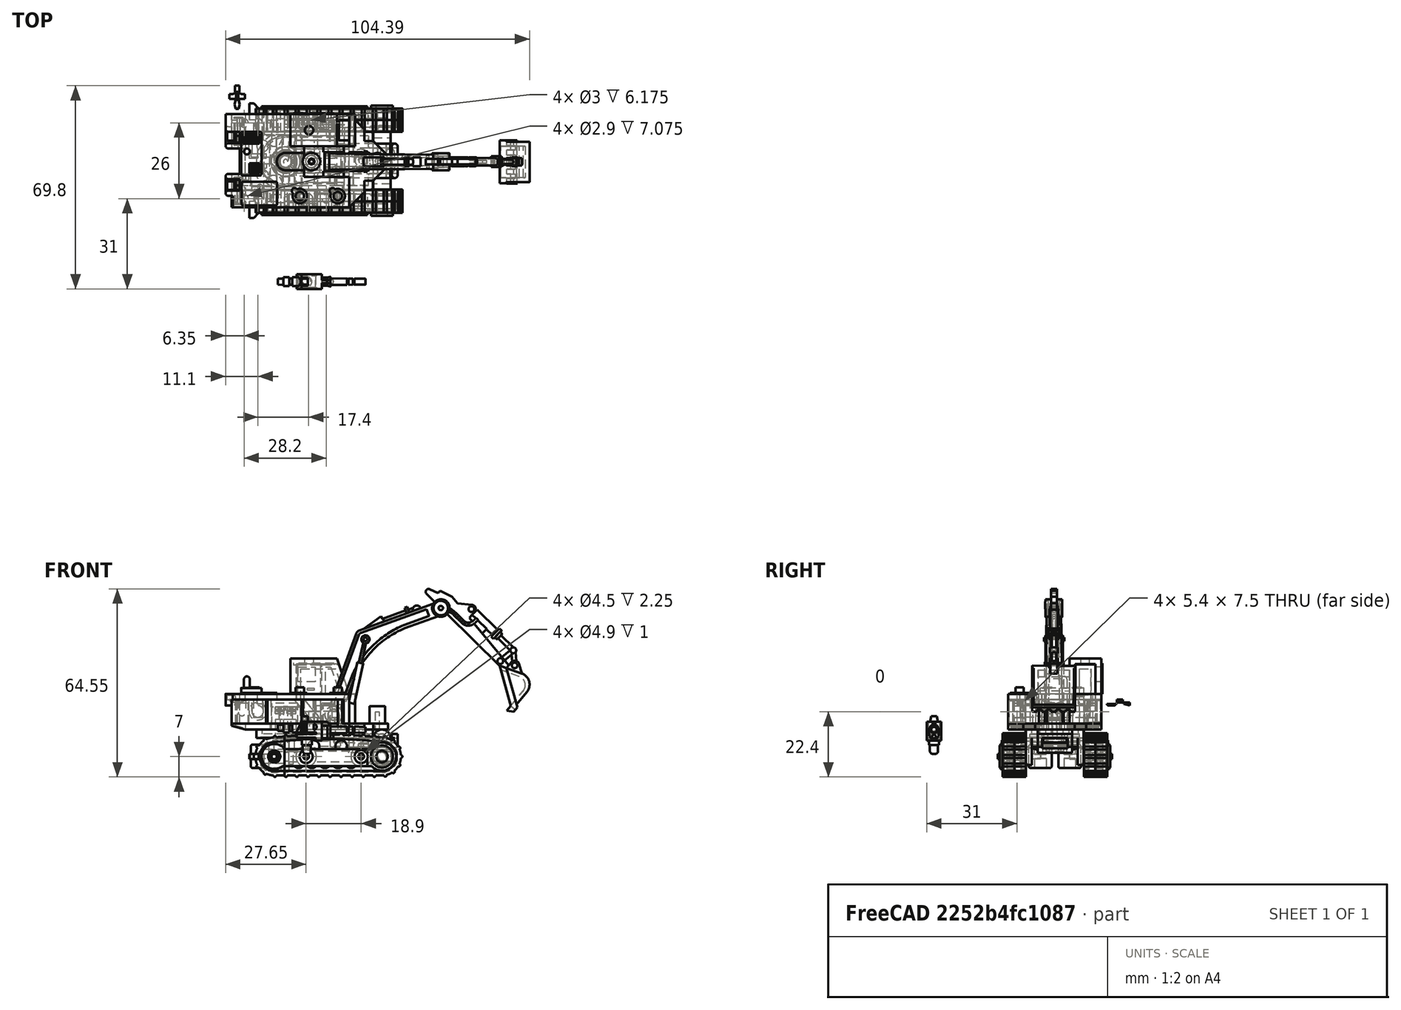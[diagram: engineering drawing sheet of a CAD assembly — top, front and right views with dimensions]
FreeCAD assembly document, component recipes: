
FREECAD ASSEMBLY — COMPONENT RECIPES ("Scavanger")

This assembly document has 15 components, labeled P0..P14 below (a component is one placed body or linked part). 15 of them carry a construction recipe — the FreeCAD feature program that regenerates the part from scratch, quoted from this document or its linked companion documents; the rest are supplied as boundary geometry only. No exploded tour is included for this assembly.
NOTE — document 3 of 4 of this assembly tour. The two overview renders and the header above are repeated from document 1; the component sections below continue where the previous document stopped.
COMPONENT P7 — recipe-attached ("Arm_Connector", modeled in this document).
Construction recipe (the document's own serialized feature program — sketch geometry with constraints, then the solid features built on it; lengths are millimeters unless a unit is written):

FEATURE [Sketcher::SketchObject] Sketch172
  ArcFitTolerance = 1e-06
  AttachmentSupport = -> [XY_Plane007]
  FullyConstrained = true
  MakeInternals = false
  MapMode = 5
  sketch-geometry (9):
    g0: LineSegment StartX=0 StartY=0 StartZ=0 EndX=18 EndY=0 EndZ=0
    g1: LineSegment StartX=18 StartY=0 StartZ=0 EndX=18 EndY=1.3 EndZ=0
    g2: LineSegment StartX=18 StartY=1.3 StartZ=0 EndX=23 EndY=1.3 EndZ=0
    g3: LineSegment StartX=23 StartY=1.3 StartZ=0 EndX=23 EndY=4.2 EndZ=0
    g4: LineSegment StartX=23 StartY=4.2 StartZ=0 EndX=16 EndY=4.2 EndZ=0
    g5: LineSegment StartX=16 StartY=4.2 StartZ=0 EndX=16 EndY=5 EndZ=0
    g6: LineSegment StartX=16 StartY=5 StartZ=0 EndX=6 EndY=2.5 EndZ=0
    g7: LineSegment StartX=6 StartY=2.5 StartZ=0 EndX=0 EndY=2.5 EndZ=0
    g8: LineSegment StartX=0 StartY=2.5 StartZ=0 EndX=0 EndY=0 EndZ=0
  constraints (27):
    c: Coincident(g0,g-1)
    c: PointOnObject(g0,g-1)
    c: Coincident(g1,g0)
    c: Vertical(g1)
    c: DistanceX(g0,g0) = 18
    c: Coincident(g2,g1)
    c: Horizontal(g2)
    c: Coincident(g3,g2)
    c: Vertical(g3)
    c: Coincident(g4,g3)
    c: Horizontal(g4)
    c: Coincident(g5,g4)
    c: Vertical(g5)
    c: Coincident(g6,g5)
    c: Coincident(g7,g6)
    c: PointOnObject(g7,g-2)
    c: Horizontal(g7)
    c: Coincident(g8,g7)
    c: Coincident(g8,g0)
    c: DistanceX(g7,g3) = 23
    c: DistanceX(g4,g4) = 7
    c: DistanceY(g3,g3) = 2.9
    c: DistanceX(g2,g2) = 5
    c: DistanceY(g1,g1) = 1.3
    c: DistanceY(g0,g5) = 5
    c: DistanceY(g8,g8) = 2.5
    c: DistanceX(g7,g7) = 6
FEATURE [PartDesign::Pad] Pad117
  Direction = (0,0,1)
  Length = 7.9
  Length2 = 10
  Profile = -> Sketch172
  ReferenceAxis = -> Sketch172 [N_Axis]
  Refine = true
  Suppressed = false
  Type = 0
FEATURE [Sketcher::SketchObject] Sketch173
  ArcFitTolerance = 1e-06
  AttachmentSupport = -> [Pad117]
  ExternalGeometry = -> [Pad117]
  FullyConstrained = true
  MakeInternals = false
  MapMode = 5
  Placement = pos=(23,0,0) rot=(0.57735,0.57735,0.57735;2.0944rad)
  sketch-geometry (8):
    g0: LineSegment StartX=1.3 StartY=0 StartZ=0 EndX=4.2 EndY=0 EndZ=0
    g1: LineSegment StartX=4.2 StartY=0 StartZ=0 EndX=4.2 EndY=1 EndZ=0
    g2: LineSegment StartX=4.2 StartY=1 StartZ=0 EndX=1.3 EndY=1 EndZ=0
    g3: LineSegment StartX=1.3 StartY=1 StartZ=0 EndX=1.3 EndY=0 EndZ=0
    g4: LineSegment StartX=1.3 StartY=7.9 StartZ=0 EndX=1.3 EndY=6.9 EndZ=0
    g5: LineSegment StartX=1.3 StartY=6.9 StartZ=0 EndX=4.2 EndY=6.9 EndZ=0
    g6: LineSegment StartX=4.2 StartY=6.9 StartZ=0 EndX=4.2 EndY=7.9 EndZ=0
    g7: LineSegment StartX=4.2 StartY=7.9 StartZ=0 EndX=1.3 EndY=7.9 EndZ=0
  constraints (22):
    c: Coincident(g0,g1)
    c: Coincident(g1,g2)
    c: Coincident(g2,g3)
    c: Coincident(g3,g0)
    c: Horizontal(g0)
    c: Horizontal(g2)
    c: Vertical(g1)
    c: Vertical(g3)
    c: Coincident(g0,g-6)
    c: PointOnObject(g1,g-3)
    c: Coincident(g4,g5)
    c: Coincident(g5,g6)
    c: Coincident(g6,g7)
    c: Coincident(g7,g4)
    c: Vertical(g4)
    c: Vertical(g6)
    c: Horizontal(g5)
    c: Horizontal(g7)
    c: Coincident(g4,g-5)
    c: PointOnObject(g5,g-3)
    c: DistanceY(g4,g4) = 1
    c: DistanceY(g3,g3) = 1
FEATURE [PartDesign::Pocket] Pocket072
  BaseFeature = -> Pad117
  Direction = (-1,0,0)
  Length = 7
  Length2 = 5
  Profile = -> Sketch173
  ReferenceAxis = -> Sketch173 [N_Axis]
  Refine = true
  Suppressed = false
  Type = 0
FEATURE [PartDesign::Pocket] Pocket073
  BaseFeature = -> Pocket072
  Direction = (0,-1,0)
  Length = 5
  Length2 = 5
  Profile = -> Pocket072 [Face9,Face7]
  Refine = true
  Suppressed = false
  Type = 0
FEATURE [Sketcher::SketchObject] Sketch174
  ArcFitTolerance = 1e-06
  AttachmentSupport = -> [Pocket073]
  ExternalGeometry = -> [Pocket073]
  FullyConstrained = true
  MakeInternals = false
  MapMode = 5
  Placement = pos=(0,0,7.9) rot=(0,0,1;0rad)
  sketch-geometry (1):
    g0: Circle CenterX=0 CenterY=0 CenterZ=0 NormalX=0 NormalY=0 NormalZ=1 AngleXU=0 Radius=1.25
  constraints (2):
    c: Coincident(g0,g-1)
    c: Radius(g0) = 1.25
FEATURE [PartDesign::Pad] Pad118
  BaseFeature = -> Pocket073
  Direction = (0,0,1)
  Length = 2
  Length2 = 10
  Profile = -> Sketch174
  ReferenceAxis = -> Sketch174 [N_Axis]
  Refine = true
  Suppressed = false
  Type = 0
FEATURE [PartDesign::Pad] Pad119
  BaseFeature = -> Pad118
  Direction = (0,0,1)
  Length = 9.9
  Length2 = 10
  Profile = -> Sketch174
  ReferenceAxis = -> Sketch174 [N_Axis]
  Refine = true
  Reversed = true
  Suppressed = false
  Type = 0
FEATURE [PartDesign::Pad] Pad120
  BaseFeature = -> Pad119
  Direction = (0,0,-1)
  Length = 0.15
  Length2 = 10
  Profile = -> Pad119 [Face9]
  Refine = true
  Suppressed = false
  Type = 0
FEATURE [PartDesign::Pad] Pad121
  BaseFeature = -> Pad120
  Direction = (0,0,1)
  Length = 0.15
  Length2 = 10
  Profile = -> Pad120 [Face1]
  Refine = true
  Suppressed = false
  Type = 0
FEATURE [Sketcher::SketchObject] Sketch175
  ArcFitTolerance = 1e-06
  AttachmentSupport = -> [Pad121]
  ExternalGeometry = -> [Pad121]
  FullyConstrained = true
  MakeInternals = false
  MapMode = 5
  Placement = pos=(0,0,0) rot=(1,0,0;1.5708rad)
  sketch-geometry (4):
    g0: LineSegment StartX=18 StartY=1 StartZ=0 EndX=18 EndY=6.9 EndZ=0
    g1: LineSegment StartX=18 StartY=6.9 StartZ=0 EndX=16 EndY=6.9 EndZ=0
    g2: LineSegment StartX=16 StartY=6.9 StartZ=0 EndX=16 EndY=1 EndZ=0
    g3: LineSegment StartX=16 StartY=1 StartZ=0 EndX=18 EndY=1 EndZ=0
  constraints (10):
    c: Coincident(g0,g1)
    c: Coincident(g1,g2)
    c: Coincident(g2,g3)
    c: Coincident(g3,g0)
    c: Vertical(g0)
    c: Vertical(g2)
    c: Horizontal(g1)
    c: Horizontal(g3)
    c: Coincident(g0,g-5)
    c: Coincident(g1,g-3)
FEATURE [PartDesign::Pocket] Pocket074
  BaseFeature = -> Pad121
  Direction = (0,1,-2e-16)
  Length = 0.3
  Length2 = 5
  Profile = -> Sketch175
  ReferenceAxis = -> Sketch175 [N_Axis]
  Refine = true
  Suppressed = false
  Type = 0
FEATURE [Sketcher::SketchObject] Sketch283
  ArcFitTolerance = 1e-06
  AttachmentSupport = -> [Pocket074]
  ExternalGeometry = -> [Pocket074]
  FullyConstrained = true
  MakeInternals = false
  MapMode = 5
  Placement = pos=(0,2.5,0) rot=(0,0.707107,0.707107;3.14159rad)
  sketch-geometry (4):
    g0: LineSegment StartX=0 StartY=-0.15 StartZ=0 EndX=0 EndY=8.05 EndZ=0
    g1: LineSegment StartX=0 StartY=8.05 StartZ=0 EndX=-9.5 EndY=8.05 EndZ=0
    g2: LineSegment StartX=-9.5 StartY=8.05 StartZ=0 EndX=-9.5 EndY=-0.15 EndZ=0
    g3: LineSegment StartX=-9.5 StartY=-0.15 StartZ=0 EndX=0 EndY=-0.15 EndZ=0
  constraints (10):
    c: Coincident(g0,g1)
    c: Coincident(g1,g2)
    c: Coincident(g2,g3)
    c: Coincident(g3,g0)
    c: Vertical(g2)
    c: Horizontal(g1)
    c: Horizontal(g3)
    c: Coincident(g0,g-4)
    c: Coincident(g0,g-3)
    c: DistanceX(g1,g1) = 9.5
FEATURE [PartDesign::Pad] Pad192
  BaseFeature = -> Pocket074
  Direction = (0,1,-2e-16)
  Length = 0.3
  Length2 = 10
  Profile = -> Sketch283
  ReferenceAxis = -> Sketch283 [N_Axis]
  Refine = true
  Suppressed = false
  Type = 0
FEATURE [PartDesign::Fillet] Fillet014
  Base = -> Pad192 [Edge38]
  BaseFeature = -> Pad192
  Radius = 0.5
  Refine = true
  SupportTransform = false
  Suppressed = false
  UseAllEdges = false
FEATURE [PartDesign::Pad] Pad193
  BaseFeature = -> Fillet014
  Direction = (0,0,-1)
  Length = 0.05
  Length2 = 10
  Profile = -> Fillet014 [Face14]
  Refine = true
  Suppressed = false
  Type = 0
FEATURE [PartDesign::Pad] Pad194
  BaseFeature = -> Pad193
  Direction = (0,0,1)
  Length = 0.05
  Length2 = 10
  Profile = -> Pad193 [Face12]
  Refine = true
  Suppressed = false
  Type = 0
FEATURE [PartDesign::Pad] Pad195
  BaseFeature = -> Pad194
  Direction = (0,1,0)
  Length = 0.3
  Length2 = 10
  Profile = -> Pad194 [Face14]
  Refine = true
  Suppressed = false
  Type = 0
FEATURE [PartDesign::Body] Body007  label="Arm_Connector"
  AllowCompound = false
  Group = -> [Sketch172,Pad117,Sketch173,Pocket072,Pocket073,Sketch174,Pad118,Pad119,Pad120,Pad121,Sketch175,Pocket074,Sketch283,Pad192,Fillet014,Pad193,Pad194,Pad195]
  Origin = -> Origin007
  Placement = pos=(39.55,-12.05,-13.2) rot=(0,-0.71,0.71;3.14159rad)
  Tip = -> Pad195
COMPONENT P8 — recipe-attached ("Waist", modeled in this document).
Construction recipe (the document's own serialized feature program — sketch geometry with constraints, then the solid features built on it; lengths are millimeters unless a unit is written):

FEATURE [Sketcher::SketchObject] Sketch176
  ArcFitTolerance = 1e-06
  AttachmentSupport = -> [XY_Plane008]
  FullyConstrained = true
  MakeInternals = false
  MapMode = 5
  sketch-geometry (1):
    g0: Circle CenterX=0 CenterY=0 CenterZ=0 NormalX=0 NormalY=0 NormalZ=1 AngleXU=0 Radius=1.5
  constraints (2):
    c: Coincident(g0,g-1)
    c: Radius(g0) = 1.5
FEATURE [PartDesign::Pad] Pad122
  Direction = (0,0,1)
  Length = 11.8
  Length2 = 10
  Profile = -> Sketch176
  ReferenceAxis = -> Sketch176 [N_Axis]
  Refine = true
  Suppressed = false
  Type = 0
FEATURE [Sketcher::SketchObject] Sketch177
  ArcFitTolerance = 1e-06
  AttachmentSupport = -> [Pad122]
  ExternalGeometry = -> [Pad122]
  FullyConstrained = true
  MakeInternals = false
  MapMode = 5
  Placement = pos=(0,0,0) rot=(1,0,0;3.14159rad)
  sketch-geometry (1):
    g0: Circle CenterX=0 CenterY=0 CenterZ=0 NormalX=0 NormalY=0 NormalZ=1 AngleXU=0 Radius=2.95
  constraints (2):
    c: Coincident(g0,g-1)
    c: Diameter(g0) = 5.9
FEATURE [PartDesign::Pad] Pad123
  BaseFeature = -> Pad122
  Direction = (0,0,-1)
  Length = 4
  Length2 = 10
  Profile = -> Sketch177
  ReferenceAxis = -> Sketch177 [N_Axis]
  Refine = true
  Suppressed = false
  Type = 0
FEATURE [Sketcher::SketchObject] Sketch178
  ArcFitTolerance = 1e-06
  AttachmentSupport = -> [Pad123]
  ExternalGeometry = -> [Pad123]
  FullyConstrained = true
  MakeInternals = false
  MapMode = 5
  Placement = pos=(0,0,11.8) rot=(0,0,1;0rad)
  sketch-geometry (1):
    g0: Circle CenterX=0 CenterY=0 CenterZ=0 NormalX=0 NormalY=0 NormalZ=1 AngleXU=0 Radius=2.95
  constraints (2):
    c: Coincident(g0,g-1)
    c: Diameter(g0) = 5.9
FEATURE [PartDesign::Pad] Pad124
  BaseFeature = -> Pad123
  Direction = (0,0,1)
  Length = 4
  Length2 = 10
  Profile = -> Sketch178
  ReferenceAxis = -> Sketch178 [N_Axis]
  Refine = true
  Suppressed = false
  Type = 0
FEATURE [Sketcher::SketchObject] Sketch179
  ArcFitTolerance = 1e-06
  AttachmentSupport = -> [Pad124]
  ExternalGeometry = -> [Pad124]
  FullyConstrained = true
  MakeInternals = false
  MapMode = 5
  Placement = pos=(0,0,15.8) rot=(0,0,1;0rad)
  sketch-geometry (6):
    g0: ArcOfCircle CenterX=0 CenterY=0 CenterZ=0 NormalX=0 NormalY=0 NormalZ=1 AngleXU=0 Radius=2.94999 StartAngle=4.71239 EndAngle=7.85398
    g1: ArcOfCircle CenterX=-6.30001 CenterY=2e-16 CenterZ=0 NormalX=0 NormalY=0 NormalZ=1 AngleXU=0 Radius=2.94999 StartAngle=1.5708 EndAngle=4.71239
    g2: LineSegment StartX=-5e-16 StartY=-2.94999 StartZ=0 EndX=-6.30001 EndY=-2.94999 EndZ=0
    g3: LineSegment StartX=9e-16 StartY=2.94999 StartZ=0 EndX=-6.30001 EndY=2.94999 EndZ=0
    g4: LineSegment [constr] StartX=-6.30001 StartY=2e-16 StartZ=0 EndX=-9.25001 EndY=2e-16 EndZ=0
    g5: LineSegment [constr] StartX=0 StartY=0 StartZ=0 EndX=2.94999 EndY=0 EndZ=0
  constraints (15):
    c: Tangent(g0,g2) = 1.5708
    c: Tangent(g0,g3) = -1.5708
    c: Tangent(g1,g2) = 1.5708
    c: Tangent(g1,g3) = -1.5708
    c: Equal(g0,g1)
    c: Horizontal(g3)
    c: Coincident(g0,g-1)
    c: Tangent(g0,g-3)
    c: Coincident(g4,g1)
    c: PointOnObject(g4,g1)
    c: Horizontal(g4)
    c: Coincident(g5,g0)
    c: PointOnObject(g5,g0)
    c: Horizontal(g5)
    c: DistanceX(g4,g5) = 12.2
FEATURE [PartDesign::Pad] Pad125
  BaseFeature = -> Pad124
  Direction = (0,0,1)
  Length = 2
  Length2 = 10
  Profile = -> Sketch179
  ReferenceAxis = -> Sketch179 [N_Axis]
  Refine = true
  Reversed = true
  Suppressed = false
  Type = 0
FEATURE [Sketcher::SketchObject] Sketch180
  ArcFitTolerance = 1e-06
  AttachmentSupport = -> [Pad125]
  ExternalGeometry = -> [Pad125]
  FullyConstrained = true
  MakeInternals = false
  MapMode = 5
  Placement = pos=(0,0,-4) rot=(1,0,0;3.14159rad)
  sketch-geometry (4):
    g0: ArcOfCircle CenterX=0 CenterY=0 CenterZ=0 NormalX=0 NormalY=0 NormalZ=1 AngleXU=0 Radius=2.95 StartAngle=4.71239 EndAngle=7.85398
    g1: ArcOfCircle CenterX=-6.30002 CenterY=1e-16 CenterZ=0 NormalX=0 NormalY=0 NormalZ=1 AngleXU=0 Radius=2.95 StartAngle=1.5708 EndAngle=4.71239
    g2: LineSegment StartX=-5e-16 StartY=-2.95 StartZ=0 EndX=-6.30002 EndY=-2.95 EndZ=0
    g3: LineSegment StartX=9e-16 StartY=2.95 StartZ=0 EndX=-6.30002 EndY=2.95 EndZ=0
  constraints (9):
    c: Tangent(g0,g2) = 1.5708
    c: Tangent(g0,g3) = -1.5708
    c: Tangent(g1,g2) = 1.5708
    c: Tangent(g1,g3) = -1.5708
    c: Equal(g0,g1)
    c: Horizontal(g3)
    c: Coincident(g0,g-1)
    c: Tangent(g0,g-3)
    c: Tangent(g1,g-4)
FEATURE [PartDesign::Pad] Pad126
  BaseFeature = -> Pad125
  Direction = (0,0,-1)
  Length = 2
  Length2 = 10
  Profile = -> Sketch180
  ReferenceAxis = -> Sketch180 [N_Axis]
  Refine = true
  Reversed = true
  Suppressed = false
  Type = 0
FEATURE [Sketcher::SketchObject] Sketch181
  ArcFitTolerance = 1e-06
  AttachmentSupport = -> [Pad126]
  ExternalGeometry = -> [Pad126]
  FullyConstrained = true
  MakeInternals = false
  MapMode = 5
  Placement = pos=(0,0,-4) rot=(1,0,0;3.14159rad)
  sketch-geometry (1):
    g0: Circle CenterX=-6.30002 CenterY=0 CenterZ=0 NormalX=0 NormalY=0 NormalZ=1 AngleXU=0 Radius=1.45
  constraints (2):
    c: Coincident(g0,g-3)
    c: Diameter(g0) = 2.9
FEATURE [PartDesign::Pad] Pad127
  BaseFeature = -> Pad126
  Direction = (0,0,-1)
  Length = 2.1
  Length2 = 10
  Profile = -> Sketch181
  ReferenceAxis = -> Sketch181 [N_Axis]
  Refine = true
  Suppressed = false
  Type = 0
FEATURE [Sketcher::SketchObject] Sketch182
  ArcFitTolerance = 1e-06
  AttachmentSupport = -> [Pad127]
  ExternalGeometry = -> [Pad127]
  FullyConstrained = true
  MakeInternals = false
  MapMode = 5
  Placement = pos=(0,0,15.8) rot=(0,0,1;0rad)
  sketch-geometry (1):
    g0: Circle CenterX=-6.30001 CenterY=0 CenterZ=0 NormalX=0 NormalY=0 NormalZ=1 AngleXU=0 Radius=1.45
  constraints (2):
    c: Coincident(g0,g-3)
    c: Diameter(g0) = 2.9
FEATURE [PartDesign::Pad] Pad128
  BaseFeature = -> Pad127
  Direction = (0,0,1)
  Length = 2.1
  Length2 = 10
  Profile = -> Sketch182
  ReferenceAxis = -> Sketch182 [N_Axis]
  Refine = true
  Suppressed = false
  Type = 0
FEATURE [Sketcher::SketchObject] Sketch183
  ArcFitTolerance = 1e-06
  AttachmentSupport = -> [Pad128]
  ExternalGeometry = -> [Pad128]
  FullyConstrained = true
  MakeInternals = false
  MapMode = 5
  Placement = pos=(0,0,17.9) rot=(0,0,1;0rad)
  sketch-geometry (4):
    g0: LineSegment StartX=-9.40001 StartY=1.6 StartZ=0 EndX=-9.40001 EndY=-1.6 EndZ=0
    g1: LineSegment StartX=-9.40001 StartY=-1.6 StartZ=0 EndX=-3.20001 EndY=-1.6 EndZ=0
    g2: LineSegment StartX=-3.20001 StartY=-1.6 StartZ=0 EndX=-3.20001 EndY=1.6 EndZ=0
    g3: LineSegment StartX=-3.20001 StartY=1.6 StartZ=0 EndX=-9.40001 EndY=1.6 EndZ=0
  constraints (12):
    c: Coincident(g0,g1)
    c: Coincident(g1,g2)
    c: Coincident(g2,g3)
    c: Coincident(g3,g0)
    c: Vertical(g0)
    c: Vertical(g2)
    c: Horizontal(g1)
    c: Horizontal(g3)
    c: DistanceX(g3,g3) = 6.2
    c: DistanceY(g0,g0) = 3.2
    c: DistanceY(g-3,g2) = 1.6
    c: DistanceX(g-3,g2) = 3.1
FEATURE [PartDesign::Pad] Pad129
  BaseFeature = -> Pad128
  Direction = (0,0,1)
  Length = 2.7
  Length2 = 10
  Profile = -> Sketch183
  ReferenceAxis = -> Sketch183 [N_Axis]
  Refine = true
  Suppressed = false
  Type = 0
FEATURE [Sketcher::SketchObject] Sketch184
  ArcFitTolerance = 1e-06
  AttachmentSupport = -> [Pad129]
  ExternalGeometry = -> [Pad129]
  FullyConstrained = true
  MakeInternals = false
  MapMode = 5
  Placement = pos=(0,0,-6.1) rot=(1,0,0;3.14159rad)
  sketch-geometry (4):
    g0: LineSegment StartX=-9.40001 StartY=1.6 StartZ=0 EndX=-9.40001 EndY=-1.6 EndZ=0
    g1: LineSegment StartX=-9.40001 StartY=-1.6 StartZ=0 EndX=-3.20001 EndY=-1.6 EndZ=0
    g2: LineSegment StartX=-3.20001 StartY=-1.6 StartZ=0 EndX=-3.20001 EndY=1.6 EndZ=0
    g3: LineSegment StartX=-3.20001 StartY=1.6 StartZ=0 EndX=-9.40001 EndY=1.6 EndZ=0
  constraints (9):
    c: Coincident(g0,g1)
    c: Coincident(g1,g2)
    c: Coincident(g2,g3)
    c: Coincident(g3,g0)
    c: Vertical(g0)
    c: Horizontal(g1)
    c: Coincident(g0,g-5)
    c: Coincident(g2,g-5)
    c: Coincident(g1,g-6)
FEATURE [PartDesign::Pad] Pad130
  BaseFeature = -> Pad129
  Direction = (0,0,-1)
  Length = 2.7
  Length2 = 10
  Profile = -> Sketch184
  ReferenceAxis = -> Sketch184 [N_Axis]
  Refine = true
  Suppressed = false
  Type = 0
FEATURE [Sketcher::SketchObject] Sketch185
  ArcFitTolerance = 1e-06
  AttachmentOffset = pos=(0,0,4.7) rot=(0,0,1;0rad)
  AttachmentSupport = -> [Pad130]
  ExternalGeometry = -> [Pad130]
  FullyConstrained = true
  MakeInternals = false
  MapMode = 5
  Placement = pos=(1.49999,0,0) rot=(0.57735,0.57735,0.57735;2.0944rad)
  sketch-geometry (4):
    g0: LineSegment StartX=-3 StartY=8.4 StartZ=0 EndX=-3 EndY=3.4 EndZ=0
    g1: LineSegment StartX=-3 StartY=3.4 StartZ=0 EndX=3 EndY=3.4 EndZ=0
    g2: LineSegment StartX=3 StartY=3.4 StartZ=0 EndX=3 EndY=8.4 EndZ=0
    g3: LineSegment StartX=3 StartY=8.4 StartZ=0 EndX=-3 EndY=8.4 EndZ=0
  constraints (12):
    c: Coincident(g0,g1)
    c: Coincident(g1,g2)
    c: Coincident(g2,g3)
    c: Coincident(g3,g0)
    c: Vertical(g0)
    c: Vertical(g2)
    c: Horizontal(g1)
    c: Horizontal(g3)
    c: DistanceX(g3,g3) = 6
    c: DistanceX(g-1,g1) = 3
    c: DistanceY(g2,g-3) = 3.4
    c: DistanceY(g-4,g1) = 3.4
FEATURE [PartDesign::Pocket] Pocket075
  BaseFeature = -> Pad130
  Direction = (-1,0,0)
  Length = 0.1
  Length2 = 5
  Profile = -> Sketch185
  ReferenceAxis = -> Sketch185 [N_Axis]
  Refine = true
  Suppressed = false
  Type = 0
FEATURE [Sketcher::SketchObject] Sketch186
  ArcFitTolerance = 1e-06
  AttachmentOffset = pos=(0,0,-7.9) rot=(0,0,1;0rad)
  AttachmentSupport = -> [Pocket075]
  ExternalGeometry = -> [Pocket075]
  FullyConstrained = true
  MakeInternals = false
  MapMode = 5
  Placement = pos=(-1.50001,0,0) rot=(0.57735,-0.57735,-0.57735;2.0944rad)
  sketch-geometry (4):
    g0: LineSegment StartX=-3 StartY=9.4 StartZ=0 EndX=-3 EndY=3.4 EndZ=0
    g1: LineSegment StartX=-3 StartY=3.4 StartZ=0 EndX=3 EndY=3.4 EndZ=0
    g2: LineSegment StartX=3 StartY=3.4 StartZ=0 EndX=3 EndY=9.4 EndZ=0
    g3: LineSegment StartX=3 StartY=9.4 StartZ=0 EndX=-3 EndY=9.4 EndZ=0
  constraints (12):
    c: Coincident(g0,g1)
    c: Coincident(g1,g2)
    c: Coincident(g2,g3)
    c: Coincident(g3,g0)
    c: Vertical(g0)
    c: Vertical(g2)
    c: Horizontal(g1)
    c: Horizontal(g3)
    c: DistanceX(g3,g3) = 6
    c: DistanceX(g-1,g1) = 3
    c: DistanceY(g2,g-4) = 2.4
    c: DistanceY(g-3,g1) = 3.4
FEATURE [PartDesign::Pocket] Pocket076
  BaseFeature = -> Pocket075
  Direction = (1,0,0)
  Length = 0.1
  Length2 = 5
  Profile = -> Sketch186
  ReferenceAxis = -> Sketch186 [N_Axis]
  Refine = true
  Suppressed = false
  Type = 0
FEATURE [PartDesign::Body] Body008  label="Waist"
  AllowCompound = false
  Group = -> [Sketch176,Pad122,Sketch177,Pad123,Sketch178,Pad124,Sketch179,Pad125,Sketch180,Pad126,Sketch181,Pad127,Sketch182,Pad128,Sketch183,Pad129,Sketch184,Pad130,Sketch185,Pocket075,Sketch186,Pocket076]
  Origin = -> Origin008
  Placement = pos=(53.7,-21.9,-13.2) rot=(0.58,0.58,0.58;4.18879rad)
  Tip = -> Pocket076
COMPONENT P9 — recipe-attached ("Pre_Right_Arm", modeled in this document).
Construction recipe (the document's own serialized feature program — sketch geometry with constraints, then the solid features built on it; lengths are millimeters unless a unit is written):

FEATURE [PartDesign::SubShapeBinder] Binder004
  BindCopyOnChange = 0
  BindMode = 2
  ClaimChildren = false
  Context = -> Body009 [Binder004.]
  Fuse = false
  MakeFace = true
  OffsetFill = false
  OffsetIntersection = false
  OffsetJoinType = 0
  OffsetOpenResult = false
  PartialLoad = false
  Refine = true
  Relative = true
  _Version = 2
FEATURE [Sketcher::SketchObject] Sketch187
  ArcFitTolerance = 1e-06
  AttachmentSupport = -> [Binder004]
  ExternalGeometry = -> [Binder004]
  FullyConstrained = true
  MakeInternals = false
  MapMode = 5
  Placement = pos=(0,-26,0) rot=(1,0,0;1.5708rad)
  sketch-geometry (4):
    g0: LineSegment StartX=2 StartY=-0.05 StartZ=0 EndX=2 EndY=-8.15 EndZ=0
    g1: LineSegment StartX=2 StartY=-8.15 StartZ=0 EndX=38.5 EndY=-8.15 EndZ=0
    g2: LineSegment StartX=38.5 StartY=-8.15 StartZ=0 EndX=38.5 EndY=-0.05 EndZ=0
    g3: LineSegment StartX=38.5 StartY=-0.05 StartZ=0 EndX=2 EndY=-0.05 EndZ=0
  constraints (12):
    c: PointOnObject(g0,g-4)
    c: PointOnObject(g0,g-4)
    c: Coincident(g1,g0)
    c: PointOnObject(g1,g-6)
    c: Horizontal(g1)
    c: Coincident(g2,g1)
    c: PointOnObject(g2,g-6)
    c: Coincident(g3,g2)
    c: Coincident(g3,g0)
    c: Horizontal(g3)
    c: DistanceY(g0,g-3) = 0.05
    c: DistanceY(g-5,g0) = 0.05
FEATURE [PartDesign::Pad] Pad131
  Direction = (0,-1,2e-16)
  Length = 6
  Length2 = 10
  Profile = -> Sketch187
  ReferenceAxis = -> Sketch187 [N_Axis]
  Refine = true
  Suppressed = false
  Type = 0
FEATURE [Sketcher::SketchObject] Sketch188
  ArcFitTolerance = 1e-06
  AttachmentSupport = -> [Pad131]
  ExternalGeometry = -> [Pad131]
  FullyConstrained = true
  MakeInternals = false
  MapMode = 5
  Placement = pos=(0,-32,1.41e-14) rot=(1,0,0;1.5708rad)
  sketch-geometry (10):
    g0: LineSegment [constr] StartX=14.1667 StartY=-0.05 StartZ=0 EndX=14.1667 EndY=-8.15 EndZ=0
    g1: LineSegment [constr] StartX=26.3333 StartY=-0.05 StartZ=0 EndX=26.3333 EndY=-8.15 EndZ=0
    g2: LineSegment StartX=14.4167 StartY=-0.05 StartZ=0 EndX=13.9167 EndY=-0.05 EndZ=0
    g3: LineSegment StartX=13.9167 StartY=-0.05 StartZ=0 EndX=13.9167 EndY=-8.15 EndZ=0
    g4: LineSegment StartX=13.9167 StartY=-8.15 StartZ=0 EndX=14.4167 EndY=-8.15 EndZ=0
    g5: LineSegment StartX=14.4167 StartY=-8.15 StartZ=0 EndX=14.4167 EndY=-0.05 EndZ=0
    g6: LineSegment StartX=26.5833 StartY=-0.05 StartZ=0 EndX=26.0833 EndY=-0.05 EndZ=0
    g7: LineSegment StartX=26.0833 StartY=-0.05 StartZ=0 EndX=26.0833 EndY=-8.15 EndZ=0
    g8: LineSegment StartX=26.0833 StartY=-8.15 StartZ=0 EndX=26.5833 EndY=-8.15 EndZ=0
    g9: LineSegment StartX=26.5833 StartY=-8.15 StartZ=0 EndX=26.5833 EndY=-0.05 EndZ=0
  constraints (33):
    c: DistanceX(g-3,g-3) = 36.5
    c: PointOnObject(g0,g-3)
    c: PointOnObject(g0,g-4)
    c: Vertical(g0)
    c: PointOnObject(g1,g-3)
    c: PointOnObject(g1,g-4)
    c: Vertical(g1)
    c: DistanceX(g-5,g0) = 12.1667
    c: DistanceX(g1,g-6) = 12.1667
    c: Coincident(g2,g3)
    c: Coincident(g3,g4)
    c: Coincident(g4,g5)
    c: Coincident(g5,g2)
    c: Horizontal(g2)
    c: Horizontal(g4)
    c: Vertical(g3)
    c: Vertical(g5)
    c: PointOnObject(g2,g-3)
    c: PointOnObject(g3,g-4)
    c: Coincident(g6,g7)
    c: Coincident(g7,g8)
    c: Coincident(g8,g9)
    c: Coincident(g9,g6)
    c: Horizontal(g6)
    c: Horizontal(g8)
    c: Vertical(g7)
    c: Vertical(g9)
    c: PointOnObject(g6,g-3)
    c: PointOnObject(g7,g-4)
    c: DistanceX(g7,g1) = 0.25
    c: DistanceX(g1,g8) = 0.25
    c: DistanceX(g0,g4) = 0.25
    c: DistanceX(g3,g0) = 0.25
FEATURE [PartDesign::Pocket] Pocket077
  BaseFeature = -> Pad131
  Direction = (0,1,-2e-16)
  Length = 0.3
  Length2 = 5
  Profile = -> Sketch188
  ReferenceAxis = -> Sketch188 [N_Axis]
  Refine = true
  Suppressed = false
  Type = 0
FEATURE [Sketcher::SketchObject] Sketch189
  ArcFitTolerance = 1e-06
  AttachmentSupport = -> [Pocket077]
  ExternalGeometry = -> [Pocket077]
  FullyConstrained = true
  MakeInternals = false
  MapMode = 5
  Placement = pos=(0,-1.8e-15,-8.15) rot=(1,0,0;3.14159rad)
  sketch-geometry (4):
    g0: LineSegment StartX=2 StartY=30 StartZ=0 EndX=4 EndY=30 EndZ=0
    g1: LineSegment StartX=4 StartY=30 StartZ=0 EndX=4 EndY=26 EndZ=0
    g2: LineSegment StartX=4 StartY=26 StartZ=0 EndX=2 EndY=26 EndZ=0
    g3: LineSegment StartX=2 StartY=26 StartZ=0 EndX=2 EndY=30 EndZ=0
  constraints (11):
    c: PointOnObject(g0,g-3)
    c: Horizontal(g0)
    c: Coincident(g1,g0)
    c: PointOnObject(g1,g-4)
    c: Vertical(g1)
    c: Coincident(g2,g1)
    c: Coincident(g2,g-4)
    c: Coincident(g3,g2)
    c: Coincident(g3,g0)
    c: DistanceY(g0,g-3) = 2
    c: DistanceX(g0,g0) = 2
FEATURE [PartDesign::Pocket] Pocket078
  BaseFeature = -> Pocket077
  Direction = (0,0,1)
  Length = 9
  Length2 = 5
  Profile = -> Sketch189
  ReferenceAxis = -> Sketch189 [N_Axis]
  Refine = true
  Suppressed = false
  Type = 0
FEATURE [Sketcher::SketchObject] Sketch190
  ArcFitTolerance = 1e-06
  AttachmentSupport = -> [Pocket078]
  ExternalGeometry = -> [Pocket078]
  FullyConstrained = true
  MakeInternals = false
  MapMode = 5
  Placement = pos=(0,-1.8e-15,-8.15) rot=(1,0,0;3.14159rad)
  sketch-geometry (8):
    g0: LineSegment StartX=13.9167 StartY=31.7 StartZ=0 EndX=13.9167 EndY=26 EndZ=0
    g1: LineSegment StartX=13.9167 StartY=26 StartZ=0 EndX=14.4167 EndY=26 EndZ=0
    g2: LineSegment StartX=14.4167 StartY=26 StartZ=0 EndX=14.4167 EndY=31.7 EndZ=0
    g3: LineSegment StartX=14.4167 StartY=31.7 StartZ=0 EndX=13.9167 EndY=31.7 EndZ=0
    g4: LineSegment StartX=26.5833 StartY=31.7 StartZ=0 EndX=26.0833 EndY=31.7 EndZ=0
    g5: LineSegment StartX=26.0833 StartY=31.7 StartZ=0 EndX=26.0833 EndY=26 EndZ=0
    g6: LineSegment StartX=26.0833 StartY=26 StartZ=0 EndX=26.5833 EndY=26 EndZ=0
    g7: LineSegment StartX=26.5833 StartY=26 StartZ=0 EndX=26.5833 EndY=31.7 EndZ=0
  constraints (20):
    c: Coincident(g0,g1)
    c: Coincident(g1,g2)
    c: Coincident(g2,g3)
    c: Coincident(g3,g0)
    c: Vertical(g0)
    c: Vertical(g2)
    c: Horizontal(g1)
    c: Coincident(g0,g-4)
    c: PointOnObject(g1,g-3)
    c: Coincident(g2,g-4)
    c: Coincident(g4,g5)
    c: Coincident(g5,g6)
    c: Coincident(g6,g7)
    c: Coincident(g7,g4)
    c: Horizontal(g6)
    c: Vertical(g5)
    c: Vertical(g7)
    c: Coincident(g4,g-5)
    c: PointOnObject(g5,g-3)
    c: Coincident(g4,g-6)
FEATURE [PartDesign::Pocket] Pocket079
  BaseFeature = -> Pocket078
  Direction = (0,0,1)
  Length = 0.3
  Length2 = 5
  Profile = -> Sketch190
  ReferenceAxis = -> Sketch190 [N_Axis]
  Refine = true
  Suppressed = false
  Type = 0
FEATURE [Sketcher::SketchObject] Sketch191
  ArcFitTolerance = 1e-06
  AttachmentSupport = -> [Pocket079]
  ExternalGeometry = -> [Pocket079]
  FullyConstrained = true
  MakeInternals = false
  MapMode = 5
  Placement = pos=(0,-26,1.14e-14) rot=(0,0.707107,0.707107;3.14159rad)
  sketch-geometry (8):
    g0: LineSegment StartX=-26.5833 StartY=-7.85 StartZ=0 EndX=-26.0833 EndY=-7.85 EndZ=0
    g1: LineSegment StartX=-26.0833 StartY=-7.85 StartZ=0 EndX=-26.0833 EndY=-0.05 EndZ=0
    g2: LineSegment StartX=-26.0833 StartY=-0.05 StartZ=0 EndX=-26.5833 EndY=-0.05 EndZ=0
    g3: LineSegment StartX=-26.5833 StartY=-0.05 StartZ=0 EndX=-26.5833 EndY=-7.85 EndZ=0
    g4: LineSegment StartX=-13.9167 StartY=-7.85 StartZ=0 EndX=-13.9167 EndY=-0.05 EndZ=0
    g5: LineSegment StartX=-13.9167 StartY=-0.05 StartZ=0 EndX=-14.4167 EndY=-0.05 EndZ=0
    g6: LineSegment StartX=-14.4167 StartY=-0.05 StartZ=0 EndX=-14.4167 EndY=-7.85 EndZ=0
    g7: LineSegment StartX=-14.4167 StartY=-7.85 StartZ=0 EndX=-13.9167 EndY=-7.85 EndZ=0
  constraints (20):
    c: Coincident(g0,g1)
    c: Coincident(g1,g2)
    c: Coincident(g2,g3)
    c: Coincident(g3,g0)
    c: Horizontal(g2)
    c: Vertical(g1)
    c: Vertical(g3)
    c: Coincident(g0,g-5)
    c: PointOnObject(g1,g-3)
    c: Coincident(g4,g5)
    c: Coincident(g5,g6)
    c: Coincident(g6,g7)
    c: Coincident(g7,g4)
    c: Vertical(g4)
    c: Vertical(g6)
    c: Horizontal(g5)
    c: Coincident(g4,g-4)
    c: PointOnObject(g5,g-3)
    c: Coincident(g6,g-4)
    c: Coincident(g0,g-5)
FEATURE [PartDesign::Pocket] Pocket080
  BaseFeature = -> Pocket079
  Direction = (0,-1,2e-16)
  Length = 0.3
  Length2 = 5
  Profile = -> Sketch191
  ReferenceAxis = -> Sketch191 [N_Axis]
  Refine = true
  Suppressed = false
  Type = 0
FEATURE [Sketcher::SketchObject] Sketch192
  ArcFitTolerance = 1e-06
  AttachmentSupport = -> [Pocket080]
  ExternalGeometry = -> [Pocket080]
  FullyConstrained = true
  MakeInternals = false
  MapMode = 5
  Placement = pos=(0,0,-0.05) rot=(0,0,1;0rad)
  sketch-geometry (8):
    g0: LineSegment StartX=26.0833 StartY=-26.3 StartZ=0 EndX=26.0833 EndY=-31.7 EndZ=0
    g1: LineSegment StartX=26.0833 StartY=-31.7 StartZ=0 EndX=26.5833 EndY=-31.7 EndZ=0
    g2: LineSegment StartX=26.5833 StartY=-31.7 StartZ=0 EndX=26.5833 EndY=-26.3 EndZ=0
    g3: LineSegment StartX=26.5833 StartY=-26.3 StartZ=0 EndX=26.0833 EndY=-26.3 EndZ=0
    g4: LineSegment StartX=13.9167 StartY=-26.3 StartZ=0 EndX=13.9167 EndY=-31.7 EndZ=0
    g5: LineSegment StartX=13.9167 StartY=-31.7 StartZ=0 EndX=14.4167 EndY=-31.7 EndZ=0
    g6: LineSegment StartX=14.4167 StartY=-31.7 StartZ=0 EndX=14.4167 EndY=-26.3 EndZ=0
    g7: LineSegment StartX=14.4167 StartY=-26.3 StartZ=0 EndX=13.9167 EndY=-26.3 EndZ=0
  constraints (20):
    c: Coincident(g0,g1)
    c: Coincident(g1,g2)
    c: Coincident(g2,g3)
    c: Coincident(g3,g0)
    c: Vertical(g0)
    c: Vertical(g2)
    c: Horizontal(g1)
    c: Horizontal(g3)
    c: Coincident(g0,g-6)
    c: Coincident(g1,g-5)
    c: Coincident(g4,g5)
    c: Coincident(g5,g6)
    c: Coincident(g6,g7)
    c: Coincident(g7,g4)
    c: Vertical(g4)
    c: Vertical(g6)
    c: Horizontal(g5)
    c: Horizontal(g7)
    c: Coincident(g4,g-3)
    c: Coincident(g5,g-4)
FEATURE [PartDesign::Pocket] Pocket081
  BaseFeature = -> Pocket080
  Direction = (0,0,-1)
  Length = 0.3
  Length2 = 5
  Profile = -> Sketch192
  ReferenceAxis = -> Sketch192 [N_Axis]
  Refine = true
  Suppressed = false
  Type = 0
FEATURE [Sketcher::SketchObject] Sketch193
  ArcFitTolerance = 1e-06
  AttachmentSupport = -> [Pocket081]
  ExternalGeometry = -> [Pocket081]
  FullyConstrained = true
  MakeInternals = false
  MapMode = 5
  Placement = pos=(0,-26,1.14e-14) rot=(0,0.707107,0.707107;3.14159rad)
  sketch-geometry (1):
    g0: Circle CenterX=-11 CenterY=-4 CenterZ=0 NormalX=0 NormalY=0 NormalZ=1 AngleXU=0 Radius=2
  constraints (4):
    c: Radius(g0) = 2
    c: DistanceY(g-4,g-4) = 8.1
    c: DistanceY(g0,g-4) = 3.95
    c: DistanceX(g0,g-7) = 9
FEATURE [PartDesign::Pad] Pad132
  BaseFeature = -> Pocket081
  Direction = (0,1,-2e-16)
  Length = 7.5
  Length2 = 10
  Profile = -> Sketch193
  ReferenceAxis = -> Sketch193 [N_Axis]
  Refine = true
  Suppressed = false
  Type = 0
FEATURE [Sketcher::SketchObject] Sketch194
  ArcFitTolerance = 1e-06
  AttachmentSupport = -> [Pad132]
  ExternalGeometry = -> [Pad132]
  FullyConstrained = true
  MakeInternals = false
  MapMode = 5
  Placement = pos=(0,-18.5,0) rot=(0,0.707107,0.707107;3.14159rad)
  sketch-geometry (1):
    g0: Circle CenterX=-11 CenterY=-4 CenterZ=0 NormalX=0 NormalY=0 NormalZ=1 AngleXU=0 Radius=3
  constraints (2):
    c: Coincident(g0,g-3)
    c: Radius(g0) = 3
FEATURE [PartDesign::Pad] Pad133
  BaseFeature = -> Pad132
  Direction = (0,1,-2e-16)
  Length = 1.5
  Length2 = 10
  Profile = -> Sketch194
  ReferenceAxis = -> Sketch194 [N_Axis]
  Refine = true
  Suppressed = false
  Type = 0
FEATURE [Sketcher::SketchObject] Sketch195
  ArcFitTolerance = 1e-06
  AttachmentSupport = -> [Pad133]
  ExternalGeometry = -> [Pad133]
  FullyConstrained = true
  MakeInternals = false
  MapMode = 5
  Placement = pos=(0,-1.8e-15,-8.15) rot=(1,0,0;3.14159rad)
  sketch-geometry (8):
    g0: Circle CenterX=6.35 CenterY=29 CenterZ=0 NormalX=0 NormalY=0 NormalZ=1 AngleXU=0 Radius=1.45
    g1: Circle CenterX=34.55 CenterY=29 CenterZ=0 NormalX=0 NormalY=0 NormalZ=1 AngleXU=0 Radius=1.45
    g2: LineSegment StartX=15.75 StartY=30.45 StartZ=0 EndX=15.75 EndY=27.55 EndZ=0
    g3: LineSegment StartX=15.75 StartY=27.55 StartZ=0 EndX=24.75 EndY=27.55 EndZ=0
    g4: LineSegment StartX=24.75 StartY=27.55 StartZ=0 EndX=24.75 EndY=30.45 EndZ=0
    g5: LineSegment StartX=24.75 StartY=30.45 StartZ=0 EndX=15.75 EndY=30.45 EndZ=0
    g6: LineSegment [constr] StartX=34.55 StartY=29 StartZ=0 EndX=36 EndY=29 EndZ=0
    g7: LineSegment [constr] StartX=6.35 StartY=29 StartZ=0 EndX=4.9 EndY=29 EndZ=0
  constraints (26):
    c: Coincident(g2,g3)
    c: Coincident(g3,g4)
    c: Coincident(g4,g5)
    c: Coincident(g5,g2)
    c: Vertical(g2)
    c: Vertical(g4)
    c: Horizontal(g3)
    c: Horizontal(g5)
    c: Radius(g0) = 1.45
    c: Radius(g1) = 1.45
    c: DistanceY(g-3,g-3) = 6
    c: DistanceY(g1,g-4) = 3
    c: DistanceY(g-8,g0) = 3
    c: Coincident(g6,g1)
    c: PointOnObject(g6,g1)
    c: Horizontal(g6)
    c: DistanceX(g6,g-4) = 2.5
    c: Coincident(g7,g0)
    c: PointOnObject(g7,g0)
    c: Horizontal(g7)
    c: DistanceX(g-6,g7) = 0.9
    c: DistanceX(g5,g5) = 9
    c: DistanceY(g2,g2) = 2.9
    c: DistanceY(g2,g-9) = 1.55
    c: DistanceX(g-10,g-10) = 11.6667
    c: DistanceX(g-10,g2) = 1.33335
FEATURE [PartDesign::Pocket] Pocket082
  BaseFeature = -> Pad133
  Direction = (0,0,1)
  Length = 7
  Length2 = 5
  Profile = -> Sketch195
  ReferenceAxis = -> Sketch195 [N_Axis]
  Refine = true
  Suppressed = false
  Type = 0
FEATURE [Sketcher::SketchObject] Sketch196
  ArcFitTolerance = 1e-06
  AttachmentSupport = -> [Pocket082]
  ExternalGeometry = -> [Pocket082]
  FullyConstrained = true
  MakeInternals = false
  MapMode = 5
  Placement = pos=(0,0,-0.05) rot=(0,0,1;0rad)
  sketch-geometry (4):
    g0: Circle CenterX=11.1 CenterY=-29 CenterZ=0 NormalX=0 NormalY=0 NormalZ=1 AngleXU=0 Radius=1.5
    g1: Circle CenterX=28.5 CenterY=-29 CenterZ=0 NormalX=0 NormalY=0 NormalZ=1 AngleXU=0 Radius=1.5
    g2: LineSegment [constr] StartX=11.1 StartY=-29 StartZ=0 EndX=9.6 EndY=-29 EndZ=0
    g3: LineSegment [constr] StartX=28.5 StartY=-29 StartZ=0 EndX=30 EndY=-29 EndZ=0
  constraints (12):
    c: Radius(g1) = 1.5
    c: Radius(g0) = 1.5
    c: DistanceY(g0,g-6) = 3
    c: DistanceY(g1,g-8) = 3
    c: Coincident(g2,g0)
    c: PointOnObject(g2,g0)
    c: Coincident(g3,g1)
    c: PointOnObject(g3,g1)
    c: Horizontal(g3)
    c: Horizontal(g2)
    c: DistanceX(g-6,g2) = 5.6
    c: DistanceX(g3,g-9) = 8.5
FEATURE [PartDesign::Pocket] Pocket083
  BaseFeature = -> Pocket082
  Direction = (0,0,-1)
  Length = 6.1
  Length2 = 5
  Profile = -> Sketch196
  ReferenceAxis = -> Sketch196 [N_Axis]
  Refine = true
  Suppressed = false
  Type = 0
FEATURE [Sketcher::SketchObject] Sketch197
  ArcFitTolerance = 1e-06
  AttachmentSupport = -> [Pocket083]
  ExternalGeometry = -> [Pocket083]
  FullyConstrained = true
  MakeInternals = false
  MapMode = 5
  Placement = pos=(0,-26,1.14e-14) rot=(0,0.707107,0.707107;3.14159rad)
  sketch-geometry (4):
    g0: LineSegment StartX=-31 StartY=-0.05 StartZ=0 EndX=-31 EndY=-8.15 EndZ=0
    g1: LineSegment StartX=-31 StartY=-8.15 StartZ=0 EndX=-30.5 EndY=-8.15 EndZ=0
    g2: LineSegment StartX=-30.5 StartY=-8.15 StartZ=0 EndX=-30.5 EndY=-0.05 EndZ=0
    g3: LineSegment StartX=-30.5 StartY=-0.05 StartZ=0 EndX=-31 EndY=-0.05 EndZ=0
  constraints (12):
    c: Coincident(g0,g1)
    c: Coincident(g1,g2)
    c: Coincident(g2,g3)
    c: Coincident(g3,g0)
    c: Vertical(g0)
    c: Vertical(g2)
    c: Horizontal(g1)
    c: Horizontal(g3)
    c: PointOnObject(g1,g-4)
    c: DistanceX(g3,g3) = 0.5
    c: DistanceX(g-5,g2) = 8
    c: PointOnObject(g2,g-3)
FEATURE [PartDesign::Pocket] Pocket084
  BaseFeature = -> Pocket083
  Direction = (0,-1,2e-16)
  Length = 1
  Length2 = 5
  Profile = -> Sketch197
  ReferenceAxis = -> Sketch197 [N_Axis]
  Refine = true
  Suppressed = false
  Type = 0
FEATURE [Sketcher::SketchObject] Sketch198
  ArcFitTolerance = 1e-06
  AttachmentSupport = -> [Pocket084]
  ExternalGeometry = -> [Pocket084]
  FullyConstrained = true
  MakeInternals = false
  MapMode = 5
  Placement = pos=(0,0,-0.05) rot=(0,0,1;0rad)
  sketch-geometry (4):
    g0: LineSegment StartX=31 StartY=-27 StartZ=0 EndX=30.5 EndY=-27 EndZ=0
    g1: LineSegment StartX=30.5 StartY=-27 StartZ=0 EndX=30.5 EndY=-32 EndZ=0
    g2: LineSegment StartX=30.5 StartY=-32 StartZ=0 EndX=31 EndY=-32 EndZ=0
    g3: LineSegment StartX=31 StartY=-32 StartZ=0 EndX=31 EndY=-27 EndZ=0
  constraints (10):
    c: Coincident(g0,g1)
    c: Coincident(g1,g2)
    c: Coincident(g2,g3)
    c: Coincident(g3,g0)
    c: Horizontal(g2)
    c: Vertical(g1)
    c: Vertical(g3)
    c: Coincident(g0,g-4)
    c: PointOnObject(g1,g-3)
    c: Coincident(g0,g-4)
FEATURE [PartDesign::Pocket] Pocket085
  BaseFeature = -> Pocket084
  Direction = (0,0,-1)
  Length = 0.5
  Length2 = 5
  Profile = -> Sketch198
  ReferenceAxis = -> Sketch198 [N_Axis]
  Refine = true
  Suppressed = false
  Type = 0
FEATURE [Sketcher::SketchObject] Sketch199
  ArcFitTolerance = 1e-06
  AttachmentSupport = -> [Pocket085]
  ExternalGeometry = -> [Pocket085]
  FullyConstrained = true
  MakeInternals = false
  MapMode = 5
  Placement = pos=(0,-1.8e-15,-8.15) rot=(1,0,0;3.14159rad)
  sketch-geometry (4):
    g0: ArcOfCircle CenterX=34.55 CenterY=29 CenterZ=0 NormalX=0 NormalY=0 NormalZ=1 AngleXU=0 Radius=3 StartAngle=4.71239 EndAngle=6.62302
    g1: LineSegment StartX=37.3784 StartY=30 StartZ=0 EndX=38.5 EndY=30 EndZ=0
    g2: LineSegment StartX=38.5 StartY=30 StartZ=0 EndX=38.5 EndY=26 EndZ=0
    g3: LineSegment StartX=38.5 StartY=26 StartZ=0 EndX=34.55 EndY=26 EndZ=0
  constraints (11):
    c: PointOnObject(g0,g-6)
    c: Coincident(g1,g0)
    c: PointOnObject(g1,g-5)
    c: Horizontal(g1)
    c: Coincident(g2,g1)
    c: Coincident(g2,g-6)
    c: Coincident(g3,g2)
    c: Tangent(g3,g0) = 1.5708
    c: Coincident(g0,g-3)
    c: DistanceY(g-5,g-5) = 6
    c: DistanceY(g1,g-5) = 2
FEATURE [PartDesign::Pocket] Pocket086
  BaseFeature = -> Pocket085
  Direction = (0,0,1)
  Length = 2
  Length2 = 5
  Profile = -> Sketch199
  ReferenceAxis = -> Sketch199 [N_Axis]
  Refine = true
  Suppressed = false
  Type = 0
FEATURE [Sketcher::SketchObject] Sketch200
  ArcFitTolerance = 1e-06
  AttachmentSupport = -> [Pocket086]
  ExternalGeometry = -> [Pocket086]
  FullyConstrained = true
  MakeInternals = false
  MapMode = 5
  Placement = pos=(38.5,0,0) rot=(0.57735,0.57735,0.57735;2.0944rad)
  sketch-geometry (4):
    g0: LineSegment StartX=-26 StartY=-4.05 StartZ=0 EndX=-26 EndY=-0.05 EndZ=0
    g1: LineSegment StartX=-26 StartY=-0.05 StartZ=0 EndX=-30 EndY=-0.05 EndZ=0
    g2: LineSegment StartX=-30 StartY=-0.05 StartZ=0 EndX=-30 EndY=-4.05 EndZ=0
    g3: LineSegment StartX=-30 StartY=-4.05 StartZ=0 EndX=-26 EndY=-4.05 EndZ=0
  constraints (11):
    c: Coincident(g0,g1)
    c: Coincident(g1,g2)
    c: Coincident(g2,g3)
    c: Coincident(g3,g0)
    c: Vertical(g0)
    c: Vertical(g2)
    c: Horizontal(g1)
    c: Horizontal(g3)
    c: Coincident(g0,g-5)
    c: DistanceX(g-4,g1) = 2
    c: Distance(g2,g-6) = 2.1
FEATURE [PartDesign::Pocket] Pocket087
  BaseFeature = -> Pocket086
  Direction = (-1,0,0)
  Length = 0.5
  Length2 = 5
  Profile = -> Sketch200
  ReferenceAxis = -> Sketch200 [N_Axis]
  Refine = true
  Suppressed = false
  Type = 0
FEATURE [Sketcher::SketchObject] Sketch201
  ArcFitTolerance = 1e-06
  AttachmentSupport = -> [Pocket087]
  ExternalGeometry = -> [Pocket087]
  FullyConstrained = true
  MakeInternals = false
  MapMode = 5
  Placement = pos=(38,0,0) rot=(0.57735,0.57735,0.57735;2.0944rad)
  sketch-geometry (4):
    g0: LineSegment StartX=-30 StartY=-0.05 StartZ=0 EndX=-30 EndY=-2.05 EndZ=0
    g1: LineSegment StartX=-30 StartY=-2.05 StartZ=0 EndX=-26 EndY=-2.05 EndZ=0
    g2: LineSegment StartX=-26 StartY=-2.05 StartZ=0 EndX=-26 EndY=-0.05 EndZ=0
    g3: LineSegment StartX=-26 StartY=-0.05 StartZ=0 EndX=-30 EndY=-0.05 EndZ=0
  constraints (11):
    c: Coincident(g0,g1)
    c: Coincident(g1,g2)
    c: Coincident(g2,g3)
    c: Coincident(g3,g0)
    c: Vertical(g0)
    c: Vertical(g2)
    c: Horizontal(g1)
    c: Horizontal(g3)
    c: Coincident(g0,g-5)
    c: PointOnObject(g1,g-3)
    c: DistanceY(g2,g2) = 2
FEATURE [PartDesign::Pocket] Pocket088
  BaseFeature = -> Pocket087
  Direction = (-1,0,0)
  Length = 0.5
  Length2 = 5
  Profile = -> Sketch201
  ReferenceAxis = -> Sketch201 [N_Axis]
  Refine = true
  Suppressed = false
  Type = 0
FEATURE [Sketcher::SketchObject] Sketch202
  ArcFitTolerance = 1e-06
  AttachmentSupport = -> [Pocket088]
  ExternalGeometry = -> [Pocket088]
  FullyConstrained = true
  MakeInternals = false
  MapMode = 5
  Placement = pos=(0,-26,1.14e-14) rot=(0,0.707107,0.707107;3.14159rad)
  sketch-geometry (4):
    g0: LineSegment StartX=-38 StartY=-4.05 StartZ=0 EndX=-31 EndY=-4.05 EndZ=0
    g1: LineSegment StartX=-31 StartY=-4.05 StartZ=0 EndX=-31 EndY=-0.05 EndZ=0
    g2: LineSegment StartX=-31 StartY=-0.05 StartZ=0 EndX=-38 EndY=-0.05 EndZ=0
    g3: LineSegment StartX=-38 StartY=-0.05 StartZ=0 EndX=-38 EndY=-4.05 EndZ=0
  constraints (10):
    c: Coincident(g0,g1)
    c: Coincident(g1,g2)
    c: Coincident(g2,g3)
    c: Coincident(g3,g0)
    c: Horizontal(g0)
    c: Horizontal(g2)
    c: Vertical(g1)
    c: Vertical(g3)
    c: Coincident(g0,g-3)
    c: Coincident(g1,g-5)
FEATURE [PartDesign::Pocket] Pocket089
  BaseFeature = -> Pocket088
  Direction = (0,-1,2e-16)
  Length = 0.5
  Length2 = 5
  Profile = -> Sketch202
  ReferenceAxis = -> Sketch202 [N_Axis]
  Refine = true
  Suppressed = false
  Type = 0
FEATURE [Sketcher::SketchObject] Sketch203
  ArcFitTolerance = 1e-06
  AttachmentSupport = -> [Pocket089]
  ExternalGeometry = -> [Pocket089]
  FullyConstrained = true
  MakeInternals = false
  MapMode = 5
  Placement = pos=(0,-26.5,0) rot=(0,0.707107,0.707107;3.14159rad)
  sketch-geometry (4):
    g0: LineSegment StartX=-37.5 StartY=-2.05 StartZ=0 EndX=-31 EndY=-2.05 EndZ=0
    g1: LineSegment StartX=-31 StartY=-2.05 StartZ=0 EndX=-31 EndY=-0.05 EndZ=0
    g2: LineSegment StartX=-31 StartY=-0.05 StartZ=0 EndX=-37.5 EndY=-0.05 EndZ=0
    g3: LineSegment StartX=-37.5 StartY=-0.05 StartZ=0 EndX=-37.5 EndY=-2.05 EndZ=0
  constraints (10):
    c: Coincident(g0,g1)
    c: Coincident(g1,g2)
    c: Coincident(g2,g3)
    c: Coincident(g3,g0)
    c: Horizontal(g0)
    c: Horizontal(g2)
    c: Vertical(g1)
    c: Vertical(g3)
    c: Coincident(g0,g-5)
    c: Coincident(g1,g-4)
FEATURE [PartDesign::Pocket] Pocket090
  BaseFeature = -> Pocket089
  Direction = (0,-1,2e-16)
  Length = 0.5
  Length2 = 5
  Profile = -> Sketch203
  ReferenceAxis = -> Sketch203 [N_Axis]
  Refine = true
  Suppressed = false
  Type = 0
FEATURE [Sketcher::SketchObject] Sketch204
  ArcFitTolerance = 1e-06
  AttachmentSupport = -> [Pocket090]
  ExternalGeometry = -> [Pocket090]
  FullyConstrained = true
  MakeInternals = false
  MapMode = 5
  Placement = pos=(0,0,-0.05) rot=(0,0,1;0rad)
  sketch-geometry (3):
    g0: LineSegment StartX=37.5 StartY=-27 StartZ=0 EndX=36.5 EndY=-27 EndZ=0
    g1: LineSegment StartX=36.5 StartY=-27 StartZ=0 EndX=37.5 EndY=-28 EndZ=0
    g2: LineSegment StartX=37.5 StartY=-28 StartZ=0 EndX=37.5 EndY=-27 EndZ=0
  constraints (8):
    c: Coincident(g0,g-4)
    c: PointOnObject(g0,g-4)
    c: Coincident(g1,g0)
    c: PointOnObject(g1,g-3)
    c: Coincident(g2,g1)
    c: Coincident(g2,g0)
    c: DistanceY(g-5,g1) = 4
    c: Angle(g2,g1) = 0.785398
FEATURE [PartDesign::Pocket] Pocket091
  BaseFeature = -> Pocket090
  Direction = (0,0,-1)
  Length = 2
  Length2 = 5
  Profile = -> Sketch204
  ReferenceAxis = -> Sketch204 [N_Axis]
  Refine = true
  Suppressed = false
  Type = 0
FEATURE [Sketcher::SketchObject] Sketch205
  ArcFitTolerance = 1e-06
  AttachmentSupport = -> [Pocket091]
  ExternalGeometry = -> [Pocket091]
  FullyConstrained = true
  MakeInternals = false
  MapMode = 5
  Placement = pos=(0,0,-2.05) rot=(0,0,1;0rad)
  sketch-geometry (3):
    g0: LineSegment StartX=38 StartY=-26.5 StartZ=0 EndX=36.5 EndY=-26.5 EndZ=0
    g1: LineSegment StartX=36.5 StartY=-26.5 StartZ=0 EndX=38 EndY=-28 EndZ=0
    g2: LineSegment StartX=38 StartY=-28 StartZ=0 EndX=38 EndY=-26.5 EndZ=0
  constraints (8):
    c: Coincident(g0,g-4)
    c: PointOnObject(g0,g-4)
    c: Coincident(g1,g0)
    c: PointOnObject(g1,g-3)
    c: Coincident(g2,g1)
    c: Coincident(g2,g0)
    c: DistanceY(g-5,g1) = 4
    c: Angle(g2,g1) = 0.785398
FEATURE [PartDesign::Pocket] Pocket092
  BaseFeature = -> Pocket091
  Direction = (0,0,-1)
  Length = 2
  Length2 = 5
  Profile = -> Sketch205
  ReferenceAxis = -> Sketch205 [N_Axis]
  Refine = true
  Suppressed = false
  Type = 0
FEATURE [Sketcher::SketchObject] Sketch206
  ArcFitTolerance = 1e-06
  AttachmentSupport = -> [Pocket092]
  ExternalGeometry = -> [Pocket092]
  FullyConstrained = true
  MakeInternals = false
  MapMode = 5
  Placement = pos=(-3.3e-15,1.15e-14,-4.05) rot=(0,0,1;0rad)
  sketch-geometry (3):
    g0: LineSegment StartX=38.5 StartY=-26 StartZ=0 EndX=38.5 EndY=-28 EndZ=0
    g1: LineSegment StartX=38.5 StartY=-28 StartZ=0 EndX=36.5 EndY=-26 EndZ=0
    g2: LineSegment StartX=38.5 StartY=-26 StartZ=0 EndX=36.5 EndY=-26 EndZ=0
  constraints (8):
    c: Coincident(g0,g-4)
    c: PointOnObject(g0,g-3)
    c: Coincident(g1,g0)
    c: PointOnObject(g1,g-4)
    c: Coincident(g2,g0)
    c: Coincident(g2,g1)
    c: DistanceY(g-5,g0) = 4
    c: Angle(g0,g1) = 0.785398
FEATURE [PartDesign::Body] Body009  label="Left_Arm"
  AllowCompound = false
  Group = -> [Binder004,Sketch187,Pad131,Sketch188,Pocket077,Sketch189,Pocket078,Sketch190,Pocket079,Sketch191,Pocket080,Sketch192,Pocket081,Sketch193,Pad132,Sketch194,Pad133,Sketch195,Pocket082,Sketch196,Pocket083,Sketch197,Pocket084,Sketch198,Pocket085,Sketch199,Pocket086,Sketch200,Pocket087,Sketch201,Pocket088,Sketch202,Pocket089,Sketch203,Pocket090,Sketch204,Pocket091,Sketch205,Pocket092,Sketch206,+17 more]
  Origin = -> Origin009
  Tip = -> Chamfer006
COMPONENT P10 — recipe-attached ("Pre_Right_Inner_Leg", modeled in this document).
Construction recipe (the document's own serialized feature program — sketch geometry with constraints, then the solid features built on it; lengths are millimeters unless a unit is written):

FEATURE [Sketcher::SketchObject] Sketch238
  ArcFitTolerance = 1e-06
  AttachmentSupport = -> [XY_Plane016]
  FullyConstrained = true
  MakeInternals = false
  MapMode = 5
  sketch-geometry (12):
    g0: ArcOfCircle CenterX=0 CenterY=0 CenterZ=0 NormalX=0 NormalY=0 NormalZ=1 AngleXU=0 Radius=6.5 StartAngle=1.66324 EndAngle=4.71239
    g1: ArcOfCircle [constr] CenterX=37 CenterY=0 CenterZ=0 NormalX=0 NormalY=0 NormalZ=1 AngleXU=0 Radius=6.5 StartAngle=4.71239 EndAngle=7.76154
    g2: LineSegment [constr] StartX=37 StartY=0 StartZ=0 EndX=37 EndY=-6.5 EndZ=0
    g3: LineSegment [constr] StartX=0 StartY=0 StartZ=0 EndX=-6.5 EndY=0 EndZ=0
    g4: LineSegment [constr] StartX=37 StartY=0 StartZ=0 EndX=43.5 EndY=0 EndZ=0
    g5: LineSegment StartX=-1.2e-15 StartY=-6.5 StartZ=0 EndX=33.5 EndY=-6.5 EndZ=0
    g6: LineSegment [constr] StartX=16.75 StartY=0 StartZ=0 EndX=16.75 EndY=-6.5 EndZ=0
    g7: LineSegment StartX=33.5 StartY=-6.5 StartZ=0 EndX=33.5 EndY=6.87017 EndZ=0
    g8: LineSegment [constr] StartX=16.75 StartY=0 StartZ=0 EndX=16.75 EndY=7.5 EndZ=0
    g9: ArcOfCircle CenterX=18.5 CenterY=-169.004 CenterZ=0 NormalX=0 NormalY=0 NormalZ=1 AngleXU=0 Radius=176.512 StartAngle=1.48571 EndAngle=1.67922
    g10: LineSegment [constr] StartX=3.5 StartY=6.87017 StartZ=0 EndX=3.5 EndY=-6.5 EndZ=0
    g11: LineSegment [constr] StartX=3.5 StartY=6.87017 StartZ=0 EndX=33.5 EndY=6.87017 EndZ=0
  constraints (41):
    c: PointOnObject(g0,g-2)
    c: Diameter(g0) = 13
    c: Coincident(g0,g-1)
    c: PointOnObject(g1,g-1)
    c: Diameter(g1) = 13
    c: Coincident(g2,g1)
    c: Coincident(g2,g1)
    c: Vertical(g2)
    c: Coincident(g3,g0)
    c: PointOnObject(g3,g0)
    c: Horizontal(g3)
    c: Coincident(g4,g1)
    c: PointOnObject(g4,g1)
    c: PointOnObject(g4,g-1)
    c: DistanceX(g3,g4) = 50
    c: DistanceX(g0,g1) = 37
    c: Coincident(g5,g0)
    c: Horizontal(g5)
    c: DistanceX(g3,g5) = 40
    c: PointOnObject(g6,g-1)
    c: Symmetric(g5,g5,g6)
    c: Vertical(g6)
    c: DistanceY(g6,g6) = 6.5
    c: Coincident(g7,g5)
    c: Vertical(g7)
    c: Coincident(g8,g6)
    c: Vertical(g8)
    c: DistanceY(g8,g8) = 7.5
    c: PointOnObject(g8,g9)
    c: Coincident(g9,g0)
    c: DistanceX(g0,g0) = 0.6
    c: PointOnObject(g10,g9)
    c: PointOnObject(g10,g5)
    c: Vertical(g10)
    c: DistanceX(g3,g10) = 10
    c: Coincident(g9,g7)
    c: Coincident(g11,g10)
    c: Coincident(g11,g7)
    c: Horizontal(g11)
    c: DistanceX(g1,g1) = 0.6
    c: DistanceY(g5,g7) = 13.3702
FEATURE [PartDesign::Pad] Pad153
  Direction = (0,0,1)
  Length = 1.5
  Length2 = 10
  Profile = -> Sketch238
  ReferenceAxis = -> Sketch238 [N_Axis]
  Refine = true
  Suppressed = false
  Type = 0
FEATURE [Sketcher::SketchObject] Sketch239
  ArcFitTolerance = 1e-06
  AttachmentSupport = -> [Pad153]
  ExternalGeometry = -> [Pad153]
  FullyConstrained = true
  MakeInternals = false
  MapMode = 5
  Placement = pos=(0,0,1.5) rot=(0,0,1;0rad)
  sketch-geometry (10):
    g0: ArcOfCircle CenterX=18.5181 CenterY=-169.001 CenterZ=0 NormalX=0 NormalY=0 NormalZ=1 AngleXU=0 Radius=175.512 StartAngle=1.48533 EndAngle=1.67941
    g1: ArcOfCircle CenterX=0 CenterY=0 CenterZ=0 NormalX=0 NormalY=0 NormalZ=1 AngleXU=0 Radius=5.5 StartAngle=1.66324 EndAngle=4.71239
    g2: LineSegment StartX=-1e-15 StartY=-5.5 StartZ=0 EndX=33.5 EndY=-5.5 EndZ=0
    g3: LineSegment [constr] StartX=0 StartY=0 StartZ=0 EndX=-0.507692 EndY=5.47652 EndZ=0
    g4: LineSegment [constr] StartX=-0.507692 StartY=5.47652 StartZ=0 EndX=-0.6 EndY=6.47225 EndZ=0
    g5: LineSegment StartX=33.5 StartY=5.87017 StartZ=0 EndX=33.5 EndY=5.37017 EndZ=0
    g6: LineSegment StartX=33.5 StartY=-5.5 StartZ=0 EndX=33.5 EndY=-5 EndZ=0
    g7: LineSegment StartX=33.5 StartY=-5 StartZ=0 EndX=0 EndY=-5 EndZ=0
    g8: ArcOfCircle CenterX=0 CenterY=0 CenterZ=0 NormalX=0 NormalY=0 NormalZ=1 AngleXU=0 Radius=5 StartAngle=1.66324 EndAngle=4.71239
    g9: ArcOfCircle CenterX=18.5272 CenterY=-169 CenterZ=0 NormalX=0 NormalY=0 NormalZ=1 AngleXU=0 Radius=175.012 StartAngle=1.48514 EndAngle=1.67951
  constraints (32):
    c: Coincident(g1,g0)
    c: PointOnObject(g1,g-2)
    c: Coincident(g2,g1)
    c: PointOnObject(g2,g-4)
    c: Horizontal(g2)
    c: PointOnObject(g0,g-4)
    c: Radius(g-6) = 6.5
    c: Radius(g1) = 5.5
    c: Coincident(g1,g-1)
    c: Coincident(g3,g1)
    c: Coincident(g3,g0)
    c: Coincident(g4,g0)
    c: Coincident(g4,g-6)
    c: Parallel(g4,g3)
    c: Radius(g-3) = 176.512
    c: Radius(g0) = 175.512
    c: DistanceY(g0,g-4) = 1
    c: Coincident(g5,g0)
    c: PointOnObject(g5,g-4)
    c: Coincident(g6,g2)
    c: PointOnObject(g6,g-4)
    c: Coincident(g7,g6)
    c: PointOnObject(g7,g-2)
    c: Horizontal(g7)
    c: Coincident(g8,g7)
    c: PointOnObject(g8,g3)
    c: Coincident(g8,g1)
    c: DistanceY(g1,g7) = 0.5
    c: DistanceY(g5,g5) = 0.5
    c: Coincident(g9,g5)
    c: Coincident(g9,g8)
    c: Radius(g9) = 175.012
FEATURE [PartDesign::Pocket] Pocket110
  BaseFeature = -> Pad153
  Direction = (0,0,-1)
  Length = 0.3
  Length2 = 5
  Profile = -> Sketch239
  ReferenceAxis = -> Sketch239 [N_Axis]
  Refine = true
  Suppressed = false
  Type = 0
FEATURE [Sketcher::SketchObject] Sketch240
  ArcFitTolerance = 1e-06
  AttachmentSupport = -> [Pocket110]
  ExternalGeometry = -> [Pocket110]
  FullyConstrained = true
  MakeInternals = false
  MapMode = 5
  Placement = pos=(0,0,0) rot=(1,0,0;3.14159rad)
  sketch-geometry (9):
    g0: LineSegment StartX=33.5 StartY=6.5 StartZ=0 EndX=0 EndY=6.5 EndZ=0
    g1: ArcOfCircle CenterX=0 CenterY=-3e-16 CenterZ=0 NormalX=0 NormalY=0 NormalZ=1 AngleXU=0 Radius=6.5 StartAngle=1.5708 EndAngle=4.61995
    g2: ArcOfCircle CenterX=18.5 CenterY=169.004 CenterZ=0 NormalX=0 NormalY=0 NormalZ=1 AngleXU=0 Radius=176.512 StartAngle=4.60397 EndAngle=4.79747
    g3: LineSegment StartX=33.5 StartY=6.5 StartZ=0 EndX=33.5 EndY=5 EndZ=0
    g4: LineSegment StartX=33.5 StartY=5 StartZ=0 EndX=0 EndY=5 EndZ=0
    g5: LineSegment StartX=33.5 StartY=-6.87017 StartZ=0 EndX=33.5 EndY=-5.37017 EndZ=0
    g6: LineSegment [constr] StartX=0 StartY=-3e-16 StartZ=0 EndX=-0.6 EndY=-6.47225 EndZ=0
    g7: ArcOfCircle CenterX=0 CenterY=-3e-16 CenterZ=0 NormalX=0 NormalY=0 NormalZ=1 AngleXU=0 Radius=5 StartAngle=1.5708 EndAngle=4.61995
    g8: ArcOfCircle CenterX=18.5272 CenterY=169 CenterZ=0 NormalX=0 NormalY=0 NormalZ=1 AngleXU=0 Radius=175.012 StartAngle=4.60368 EndAngle=4.79805
  constraints (24):
    c: Coincident(g0,g-4)
    c: Coincident(g0,g-6)
    c: Coincident(g1,g0)
    c: Tangent(g1,g-6) = -1.5708
    c: Coincident(g2,g1)
    c: Tangent(g2,g-5) = -1.5708
    c: Coincident(g3,g0)
    c: PointOnObject(g3,g-4)
    c: Coincident(g4,g3)
    c: PointOnObject(g4,g-2)
    c: Horizontal(g4)
    c: DistanceY(g3,g3) = 1.5
    c: Coincident(g5,g2)
    c: PointOnObject(g5,g-4)
    c: DistanceY(g5,g5) = 1.5
    c: Coincident(g6,g1)
    c: Coincident(g6,g1)
    c: Coincident(g7,g4)
    c: PointOnObject(g7,g6)
    c: Coincident(g7,g1)
    c: Coincident(g8,g7)
    c: Coincident(g8,g5)
    c: Radius(g2) = 176.512
    c: Radius(g8) = 175.012
FEATURE [PartDesign::Pad] Pad154
  BaseFeature = -> Pocket110
  Direction = (0,0,-1)
  Length = 2.5
  Length2 = 10
  Profile = -> Sketch240
  ReferenceAxis = -> Sketch240 [N_Axis]
  Refine = true
  Suppressed = false
  Type = 0
FEATURE [Sketcher::SketchObject] Sketch241
  ArcFitTolerance = 1e-06
  AttachmentSupport = -> [Pad154]
  ExternalGeometry = -> [Pad154]
  FullyConstrained = true
  MakeInternals = false
  MapMode = 5
  Placement = pos=(0,0,-2.5) rot=(1,0,0;3.14159rad)
  sketch-geometry (61):
    g0: ArcOfCircle CenterX=33.0017 CenterY=-6.91196 CenterZ=0 NormalX=0 NormalY=0 NormalZ=1 AngleXU=0 Radius=0.5 StartAngle=3.22243 EndAngle=6.36685
    g1: ArcOfCircle CenterX=25.4163 CenterY=-7.37312 CenterZ=0 NormalX=0 NormalY=0 NormalZ=1 AngleXU=0 Radius=0.5 StartAngle=3.17937 EndAngle=6.32379
    g2: ArcOfCircle CenterX=29.2115 CenterY=-7.18337 CenterZ=0 NormalX=0 NormalY=0 NormalZ=1 AngleXU=0 Radius=0.5 StartAngle=3.2009 EndAngle=6.34532
    g3: ArcOfCircle CenterX=10.221 CenterY=-7.31441 CenterZ=0 NormalX=0 NormalY=0 NormalZ=1 AngleXU=0 Radius=0.5 StartAngle=3.09326 EndAngle=6.23768
    g4: ArcOfCircle CenterX=2.6393 CenterY=-6.79464 CenterZ=0 NormalX=0 NormalY=0 NormalZ=1 AngleXU=0 Radius=0.5 StartAngle=3.0502 EndAngle=6.19462
    g5: ArcOfCircle CenterX=21.6179 CenterY=-7.48114 CenterZ=0 NormalX=0 NormalY=0 NormalZ=1 AngleXU=0 Radius=0.5 StartAngle=3.15784 EndAngle=6.30227
    g6: ArcOfCircle CenterX=17.818 CenterY=-7.50736 CenterZ=0 NormalX=0 NormalY=0 NormalZ=1 AngleXU=0 Radius=0.5 StartAngle=3.13631 EndAngle=6.28074
    g7: ArcOfCircle CenterX=14.0184 CenterY=-7.45177 CenterZ=0 NormalX=0 NormalY=0 NormalZ=1 AngleXU=0 Radius=0.5 StartAngle=3.11478 EndAngle=6.25921
    g8: ArcOfCircle CenterX=6.42734 CenterY=-7.09533 CenterZ=0 NormalX=0 NormalY=0 NormalZ=1 AngleXU=0 Radius=0.5 StartAngle=3.07173 EndAngle=6.21615
    g9: ArcOfCircle CenterX=-1.15373 CenterY=-6.39679 CenterZ=0 NormalX=0 NormalY=0 NormalZ=1 AngleXU=0 Radius=0.5 StartAngle=2.92468 EndAngle=6.14321
    g10: ArcOfCircle CenterX=33 CenterY=6.5 CenterZ=0 NormalX=0 NormalY=0 NormalZ=1 AngleXU=0 Radius=0.5 StartAngle=4e-16 EndAngle=3.14159
    g11: ArcOfCircle CenterX=29.2105 CenterY=6.5 CenterZ=0 NormalX=0 NormalY=0 NormalZ=1 AngleXU=0 Radius=0.5 StartAngle=0 EndAngle=3.14159
    g12: ArcOfCircle CenterX=25.4159 CenterY=6.5 CenterZ=0 NormalX=0 NormalY=0 NormalZ=1 AngleXU=0 Radius=0.5 StartAngle=-9e-16 EndAngle=3.14159
    g13: ArcOfCircle CenterX=21.6178 CenterY=6.5 CenterZ=0 NormalX=0 NormalY=0 NormalZ=1 AngleXU=0 Radius=0.5 StartAngle=3e-16 EndAngle=3.14159
    g14: ArcOfCircle CenterX=17.818 CenterY=6.5 CenterZ=0 NormalX=0 NormalY=0 NormalZ=1 AngleXU=0 Radius=0.5 StartAngle=0 EndAngle=3.14159
    g15: ArcOfCircle CenterX=14.0183 CenterY=6.5 CenterZ=0 NormalX=0 NormalY=0 NormalZ=1 AngleXU=0 Radius=0.5 StartAngle=0 EndAngle=3.14159
    g16: ArcOfCircle CenterX=10.2205 CenterY=6.5 CenterZ=0 NormalX=0 NormalY=0 NormalZ=1 AngleXU=0 Radius=0.5 StartAngle=2e-16 EndAngle=3.14159
    g17: ArcOfCircle CenterX=6.42621 CenterY=6.5 CenterZ=0 NormalX=0 NormalY=0 NormalZ=1 AngleXU=0 Radius=0.5 StartAngle=3e-16 EndAngle=3.14159
    g18: ArcOfCircle CenterX=2.63734 CenterY=6.5 CenterZ=0 NormalX=0 NormalY=0 NormalZ=1 AngleXU=0 Radius=0.5 StartAngle=0 EndAngle=3.14159
    g19: ArcOfCircle CenterX=-1.15373 CenterY=6.39679 CenterZ=0 NormalX=0 NormalY=0 NormalZ=1 AngleXU=0 Radius=0.5 StartAngle=0.139971 EndAngle=3.35851
    g20: LineSegment [constr] StartX=29.7105 StartY=-7.15232 StartZ=0 EndX=29.7105 EndY=6.5 EndZ=0
    g21: LineSegment [constr] StartX=25.9159 StartY=-7.35282 StartZ=0 EndX=25.9159 EndY=6.5 EndZ=0
    g22: LineSegment [constr] StartX=22.1178 StartY=-7.4716 StartZ=0 EndX=22.1178 EndY=6.5 EndZ=0
    g23: LineSegment [constr] StartX=18.318 StartY=-7.50858 StartZ=0 EndX=18.318 EndY=6.5 EndZ=0
    g24: LineSegment [constr] StartX=14.5183 StartY=-7.46376 StartZ=0 EndX=14.5183 EndY=6.5 EndZ=0
    g25: LineSegment [constr] StartX=10.7205 StartY=-7.33716 StartZ=0 EndX=10.7205 EndY=6.5 EndZ=0
    g26: LineSegment [constr] StartX=6.92621 StartY=-7.12882 StartZ=0 EndX=6.92621 EndY=6.5 EndZ=0
    g27: LineSegment [constr] StartX=3.13734 StartY=-6.83886 StartZ=0 EndX=3.13734 EndY=6.5 EndZ=0
    g28: LineSegment [constr] StartX=-0.658617 StartY=-6.46655 StartZ=0 EndX=-0.658617 EndY=6.46655 EndZ=0
    g29: ArcOfCircle CenterX=-6.5 CenterY=0 CenterZ=0 NormalX=0 NormalY=0 NormalZ=1 AngleXU=0 Radius=0.5 StartAngle=1.53233 EndAngle=4.75086
    g30: ArcOfCircle CenterX=-3.88826 CenterY=5.20878 CenterZ=0 NormalX=0 NormalY=0 NormalZ=1 AngleXU=0 Radius=0.5 StartAngle=0.602774 EndAngle=3.82131
    g31: ArcOfCircle CenterX=-5.80474 CenterY=2.9249 CenterZ=0 NormalX=0 NormalY=0 NormalZ=1 AngleXU=0 Radius=0.5 StartAngle=1.06558 EndAngle=4.28411
    g32: ArcOfCircle CenterX=-3.88826 CenterY=-5.20878 CenterZ=0 NormalX=0 NormalY=0 NormalZ=1 AngleXU=0 Radius=0.5 StartAngle=2.46188 EndAngle=5.68041
    g33: ArcOfCircle CenterX=-5.80474 CenterY=-2.9249 CenterZ=0 NormalX=0 NormalY=0 NormalZ=1 AngleXU=0 Radius=0.5 StartAngle=1.99907 EndAngle=5.21761
    g34: LineSegment [constr] StartX=-3.47638 StartY=-5.49225 StartZ=0 EndX=-3.47638 EndY=5.49225 EndZ=0
    g35: LineSegment [constr] StartX=-5.56274 StartY=-3.36243 StartZ=0 EndX=-5.56274 EndY=3.36243 EndZ=0
    g36: LineSegment StartX=33.5 StartY=-6.87017 StartZ=0 EndX=32.5034 EndY=-6.95233 EndZ=0
    g37: LineSegment StartX=29.7105 StartY=-7.15232 StartZ=0 EndX=28.7124 EndY=-7.213 EndZ=0
    g38: LineSegment StartX=25.9159 StartY=-7.35282 StartZ=0 EndX=24.9166 EndY=-7.39201 EndZ=0
    g39: LineSegment StartX=22.1178 StartY=-7.4716 StartZ=0 EndX=21.1179 EndY=-7.48926 EndZ=0
    g40: LineSegment StartX=18.318 StartY=-7.50858 StartZ=0 EndX=17.318 EndY=-7.50472 EndZ=0
    g41: LineSegment StartX=14.5183 StartY=-7.46376 StartZ=0 EndX=13.5186 EndY=-7.43837 EndZ=0
    g42: LineSegment StartX=10.7205 StartY=-7.33716 StartZ=0 EndX=9.72156 EndY=-7.29025 EndZ=0
    g43: LineSegment StartX=6.92621 StartY=-7.12882 StartZ=0 EndX=5.92856 EndY=-7.06043 EndZ=0
    g44: LineSegment StartX=3.13734 StartY=-6.83886 StartZ=0 EndX=2.14138 EndY=-6.74901 EndZ=0
    g45: LineSegment StartX=-0.658617 StartY=-6.46655 StartZ=0 EndX=-1.64201 EndY=-6.28918 EndZ=0
    g46: LineSegment StartX=-3.47638 StartY=-5.49225 StartZ=0 EndX=-4.27713 EndY=-4.8945 EndZ=0
    g47: LineSegment StartX=-5.56274 StartY=-3.36243 StartZ=0 EndX=-6.01239 EndY=-2.47006 EndZ=0
    g48: LineSegment StartX=-6.48077 StartY=-0.49963 StartZ=0 EndX=-6.48077 EndY=0.49963 EndZ=0
    g49: LineSegment StartX=-6.01239 StartY=2.47006 StartZ=0 EndX=-5.56274 EndY=3.36243 EndZ=0
    g50: LineSegment StartX=-4.27713 StartY=4.8945 StartZ=0 EndX=-3.47638 EndY=5.49225 EndZ=0
    g51: LineSegment StartX=-1.64201 StartY=6.28918 StartZ=0 EndX=-0.658617 EndY=6.46655 EndZ=0
    g52: LineSegment StartX=2.13734 StartY=6.5 StartZ=0 EndX=3.13734 EndY=6.5 EndZ=0
    g53: LineSegment StartX=5.92621 StartY=6.5 StartZ=0 EndX=6.92621 EndY=6.5 EndZ=0
    g54: LineSegment StartX=9.72046 StartY=6.5 StartZ=0 EndX=10.7205 EndY=6.5 EndZ=0
    g55: LineSegment StartX=13.5183 StartY=6.5 StartZ=0 EndX=14.5183 EndY=6.5 EndZ=0
    g56: LineSegment StartX=17.318 StartY=6.5 StartZ=0 EndX=18.318 EndY=6.5 EndZ=0
    g57: LineSegment StartX=21.1178 StartY=6.5 StartZ=0 EndX=22.1178 EndY=6.5 EndZ=0
    g58: LineSegment StartX=24.9159 StartY=6.5 StartZ=0 EndX=25.9159 EndY=6.5 EndZ=0
    g59: LineSegment StartX=28.7105 StartY=6.5 StartZ=0 EndX=29.7105 EndY=6.5 EndZ=0
    g60: LineSegment StartX=32.5 StartY=6.5 StartZ=0 EndX=33.5 EndY=6.5 EndZ=0
  constraints (196):
    c: Coincident(g0,g-3)
    c: PointOnObject(g0,g-3)
    c: PointOnObject(g1,g-3)
    c: PointOnObject(g1,g-3)
    c: PointOnObject(g2,g-3)
    c: PointOnObject(g2,g-3)
    c: PointOnObject(g3,g-3)
    c: PointOnObject(g3,g-3)
    c: PointOnObject(g4,g-3)
    c: PointOnObject(g4,g-3)
    c: PointOnObject(g0,g-3)
    c: PointOnObject(g1,g-3)
    c: PointOnObject(g2,g-3)
    c: PointOnObject(g3,g-3)
    c: PointOnObject(g4,g-3)
    c: Diameter(g0) = 1
    c: Diameter(g1) = 1
    c: Diameter(g2) = 1
    c: Diameter(g3) = 1
    c: Diameter(g4) = 1
    c: Diameter(g5) = 1
    c: PointOnObject(g5,g-3)
    c: PointOnObject(g5,g-3)
    c: PointOnObject(g5,g-3)
    c: PointOnObject(g6,g-3)
    c: PointOnObject(g6,g-3)
    c: PointOnObject(g7,g-3)
    c: PointOnObject(g7,g-3)
    c: PointOnObject(g6,g-3)
    c: PointOnObject(g7,g-3)
    c: Diameter(g7) = 1
    c: Diameter(g6) = 1
    c: PointOnObject(g8,g-3)
    c: PointOnObject(g8,g-3)
    c: PointOnObject(g8,g-3)
    c: Diameter(g8) = 1
    c: Distance(g0,g2) = 2.8
    c: Distance(g2,g1) = 2.8
    c: Distance(g1,g5) = 2.8
    c: Distance(g5,g6) = 2.8
    c: Distance(g6,g7) = 2.8
    c: Distance(g7,g3) = 2.8
    c: Distance(g3,g8) = 2.8
    c: Distance(g8,g4) = 2.8
    c: Diameter(g9) = 1
    c: DistanceX(g9,g4) = 2.8
    c: PointOnObject(g9,g-5)
    c: PointOnObject(g9,g-5)
    c: PointOnObject(g9,g-5)
    c: Coincident(g10,g-4)
    c: PointOnObject(g10,g-4)
    c: PointOnObject(g11,g-4)
    c: PointOnObject(g11,g-4)
    c: PointOnObject(g12,g-4)
    c: PointOnObject(g12,g-4)
    c: PointOnObject(g13,g-4)
    c: PointOnObject(g13,g-4)
    c: PointOnObject(g14,g-4)
    c: PointOnObject(g14,g-4)
    c: PointOnObject(g15,g-4)
    c: PointOnObject(g15,g-4)
    c: PointOnObject(g16,g-4)
    c: PointOnObject(g16,g-4)
    c: PointOnObject(g17,g-4)
    c: PointOnObject(g17,g-4)
    c: PointOnObject(g18,g-4)
    c: PointOnObject(g18,g-4)
    c: PointOnObject(g10,g-4)
    c: PointOnObject(g11,g-4)
    c: PointOnObject(g12,g-4)
    c: PointOnObject(g13,g-4)
    c: PointOnObject(g14,g-4)
    c: PointOnObject(g15,g-4)
    c: PointOnObject(g16,g-4)
    c: PointOnObject(g17,g-4)
    c: PointOnObject(g18,g-4)
    c: Diameter(g10) = 1
    c: Diameter(g11) = 1
    c: Diameter(g12) = 1
    c: Diameter(g13) = 1
    c: Diameter(g14) = 1
    c: Diameter(g15) = 1
    c: Diameter(g16) = 1
    c: Diameter(g17) = 1
    c: Diameter(g18) = 1
    c: Diameter(g19) = 1
    c: Coincident(g20,g2)
    c: Coincident(g20,g11)
    c: Vertical(g20)
    c: Coincident(g21,g1)
    c: Coincident(g21,g12)
    c: Vertical(g21)
    c: Coincident(g22,g5)
    c: Coincident(g22,g13)
    c: Vertical(g22)
    c: Coincident(g23,g6)
    c: Coincident(g23,g14)
    c: Vertical(g23)
    c: Coincident(g24,g7)
    c: Coincident(g24,g15)
    c: Vertical(g24)
    c: Coincident(g25,g3)
    c: Coincident(g25,g16)
    c: Vertical(g25)
    c: Coincident(g26,g8)
    c: Coincident(g26,g17)
    c: Vertical(g26)
    c: Coincident(g27,g4)
    c: Coincident(g27,g18)
    c: Vertical(g27)
    c: PointOnObject(g19,g-5)
    c: PointOnObject(g19,g-5)
    c: PointOnObject(g19,g-5)
    c: Coincident(g28,g9)
    c: Coincident(g28,g19)
    c: Vertical(g28)
    c: PointOnObject(g29,g-5)
    c: PointOnObject(g29,g-5)
    c: PointOnObject(g29,g-1)
    c: PointOnObject(g29,g-5)
    c: Diameter(g29) = 1
    c: PointOnObject(g30,g-5)
    c: PointOnObject(g30,g-5)
    c: PointOnObject(g31,g-5)
    c: PointOnObject(g31,g-5)
    c: PointOnObject(g32,g-5)
    c: PointOnObject(g32,g-5)
    c: PointOnObject(g33,g-5)
    c: PointOnObject(g33,g-5)
    c: PointOnObject(g32,g-5)
    c: PointOnObject(g33,g-5)
    c: PointOnObject(g31,g-5)
    c: PointOnObject(g30,g-5)
    c: Diameter(g30) = 1
    c: Diameter(g31) = 1
    c: Diameter(g33) = 1
    c: Diameter(g32) = 1
    c: Distance(g9,g32) = 2
    c: Distance(g32,g33) = 2
    c: Distance(g33,g29) = 2.02533
    c: Coincident(g34,g32)
    c: Coincident(g34,g30)
    c: Coincident(g35,g33)
    c: Coincident(g35,g31)
    c: Vertical(g35)
    c: Vertical(g34)
    c: Coincident(g0,g36)
    c: Coincident(g36,g0)
    c: Coincident(g60,g10)
    c: Coincident(g60,g10)
    c: Coincident(g59,g11)
    c: Coincident(g59,g11)
    c: Coincident(g58,g12)
    c: Coincident(g58,g12)
    c: Coincident(g13,g57)
    c: Coincident(g57,g13)
    c: Coincident(g56,g14)
    c: Coincident(g56,g14)
    c: Coincident(g55,g15)
    c: Coincident(g55,g15)
    c: Coincident(g54,g16)
    c: Coincident(g54,g16)
    c: Coincident(g53,g17)
    c: Coincident(g53,g17)
    c: Coincident(g52,g18)
    c: Coincident(g52,g18)
    c: Coincident(g51,g19)
    c: Coincident(g51,g19)
    c: Coincident(g50,g30)
    c: Coincident(g50,g30)
    c: Coincident(g49,g31)
    c: Coincident(g49,g31)
    c: Coincident(g48,g29)
    c: Coincident(g48,g29)
    c: Coincident(g47,g33)
    c: Coincident(g47,g33)
    c: Coincident(g46,g32)
    c: Coincident(g46,g32)
    c: Coincident(g45,g9)
    c: Coincident(g45,g9)
    c: Coincident(g44,g4)
    c: Coincident(g44,g4)
    c: Coincident(g43,g8)
    c: Coincident(g43,g8)
    c: Coincident(g42,g3)
    c: Coincident(g42,g3)
    c: Coincident(g41,g7)
    c: Coincident(g41,g7)
    c: Coincident(g40,g6)
    c: Coincident(g40,g6)
    c: Coincident(g39,g5)
    c: Coincident(g39,g5)
    c: Coincident(g37,g2)
    c: Coincident(g37,g2)
    c: Coincident(g38,g1)
    c: Coincident(g38,g1)
FEATURE [PartDesign::Pad] Pad155
  BaseFeature = -> Pad154
  Direction = (0,0,-1)
  Length = 4
  Length2 = 10
  Profile = -> Sketch241
  ReferenceAxis = -> Sketch241 [N_Axis]
  Refine = true
  Reversed = true
  Suppressed = false
  Type = 0
FEATURE [Sketcher::SketchObject] Sketch242
  ArcFitTolerance = 1e-06
  AttachmentSupport = -> [Pad155]
  ExternalGeometry = -> [Pad155]
  FullyConstrained = true
  MakeInternals = false
  MapMode = 5
  Placement = pos=(0,0,0) rot=(1,0,0;3.14159rad)
  sketch-geometry (4):
    g0: ArcOfCircle CenterX=18.5272 CenterY=169 CenterZ=0 NormalX=0 NormalY=0 NormalZ=1 AngleXU=0 Radius=175.012 StartAngle=4.78945 EndAngle=4.79805
    g1: LineSegment StartX=33.5 StartY=-5.37017 StartZ=0 EndX=33.5 EndY=5 EndZ=0
    g2: LineSegment StartX=33.5 StartY=5 StartZ=0 EndX=32 EndY=5 EndZ=0
    g3: LineSegment StartX=32 StartY=5 StartZ=0 EndX=32 EndY=-5.49248 EndZ=0
  constraints (10):
    c: Tangent(g0,g-5) = -1.5708
    c: PointOnObject(g0,g-5)
    c: Coincident(g1,g0)
    c: Coincident(g1,g-4)
    c: Coincident(g2,g1)
    c: PointOnObject(g2,g-3)
    c: Coincident(g3,g2)
    c: Coincident(g3,g0)
    c: Vertical(g3)
    c: DistanceX(g2,g2) = 1.5
FEATURE [PartDesign::Pad] Pad156
  BaseFeature = -> Pad155
  Direction = (0,0,-1)
  Length = 2.5
  Length2 = 10
  Profile = -> Sketch242
  ReferenceAxis = -> Sketch242 [N_Axis]
  Refine = true
  Suppressed = false
  Type = 0
FEATURE [Sketcher::SketchObject] Sketch243
  ArcFitTolerance = 1e-06
  AttachmentSupport = -> [Pad156]
  ExternalGeometry = -> [Pad156]
  FullyConstrained = true
  MakeInternals = false
  MapMode = 5
  Placement = pos=(33.5,-3.69e-14,1.3e-13) rot=(0.57735,0.57735,0.57735;2.0944rad)
  sketch-geometry (2):
    g0: ArcOfCircle CenterX=0 CenterY=-2.5 CenterZ=0 NormalX=0 NormalY=0 NormalZ=1 AngleXU=0 Radius=1.5 StartAngle=0 EndAngle=3.14159
    g1: LineSegment StartX=-1.5 StartY=-2.5 StartZ=0 EndX=1.5 EndY=-2.5 EndZ=0
  constraints (7):
    c: PointOnObject(g0,g-3)
    c: PointOnObject(g0,g-3)
    c: PointOnObject(g0,g-3)
    c: PointOnObject(g0,g-2)
    c: Radius(g0) = 1.5
    c: Coincident(g1,g0)
    c: Coincident(g1,g0)
FEATURE [PartDesign::Pocket] Pocket111
  BaseFeature = -> Pad156
  Direction = (-1,1.1e-15,-3.8e-15)
  Length = 5
  Length2 = 5
  Profile = -> Sketch243
  ReferenceAxis = -> Sketch243 [N_Axis]
  Refine = true
  Suppressed = false
  Type = 0
FEATURE [Sketcher::SketchObject] Sketch244
  ArcFitTolerance = 1e-06
  AttachmentSupport = -> [Pocket111]
  ExternalGeometry = -> [Pocket111]
  FullyConstrained = true
  MakeInternals = false
  MapMode = 5
  Placement = pos=(0,0,0) rot=(1,0,0;3.14159rad)
  sketch-geometry (8):
    g0: LineSegment StartX=-3.15 StartY=1.65 StartZ=0 EndX=-3.15 EndY=-1.65 EndZ=0
    g1: LineSegment StartX=-3.15 StartY=-1.65 StartZ=0 EndX=3.15 EndY=-1.65 EndZ=0
    g2: LineSegment StartX=3.15 StartY=-1.65 StartZ=0 EndX=3.15 EndY=1.65 EndZ=0
    g3: LineSegment StartX=3.15 StartY=1.65 StartZ=0 EndX=-3.15 EndY=1.65 EndZ=0
    g4: Circle CenterX=7.15 CenterY=0 CenterZ=0 NormalX=0 NormalY=0 NormalZ=1 AngleXU=0 Radius=2.25
    g5: Circle CenterX=26.05 CenterY=0 CenterZ=0 NormalX=0 NormalY=0 NormalZ=1 AngleXU=0 Radius=2.25
    g6: LineSegment [constr] StartX=26.05 StartY=0 StartZ=0 EndX=28.3 EndY=0 EndZ=0
    g7: LineSegment [constr] StartX=7.15 StartY=0 StartZ=0 EndX=4.9 EndY=0 EndZ=0
  constraints (24):
    c: Coincident(g0,g1)
    c: Coincident(g1,g2)
    c: Coincident(g2,g3)
    c: Coincident(g3,g0)
    c: Vertical(g0)
    c: Vertical(g2)
    c: Horizontal(g1)
    c: Horizontal(g3)
    c: PointOnObject(g4,g-1)
    c: PointOnObject(g5,g-1)
    c: Diameter(g4) = 4.5
    c: Diameter(g5) = 4.5
    c: DistanceX(g3,g3) = 6.3
    c: DistanceY(g2,g2) = 3.3
    c: DistanceX(g0,g-1) = 3.15
    c: Coincident(g6,g5)
    c: PointOnObject(g6,g5)
    c: Horizontal(g6)
    c: DistanceX(g6,g-3) = 5.2
    c: Coincident(g7,g4)
    c: PointOnObject(g7,g4)
    c: Horizontal(g7)
    c: DistanceX(g7,g6) = 23.4
    c: DistanceY(g1,g-1) = 1.65
FEATURE [PartDesign::Pocket] Pocket112
  BaseFeature = -> Pocket111
  Direction = (0,0,1)
  Length = 5
  Length2 = 5
  Profile = -> Sketch244 [Edge4,Edge1,Edge2,Edge3]
  ReferenceAxis = -> Sketch244 [N_Axis]
  Refine = true
  Suppressed = false
  Type = 0
FEATURE [PartDesign::Pad] Pad157
  BaseFeature = -> Pocket112
  Direction = (0,0,-1)
  Length = 4
  Length2 = 10
  Profile = -> Sketch244 [Edge5,Edge6]
  ReferenceAxis = -> Sketch244 [N_Axis]
  Refine = true
  Suppressed = false
  Type = 0
FEATURE [Sketcher::SketchObject] Sketch245
  ArcFitTolerance = 1e-06
  AttachmentSupport = -> [Pad157]
  ExternalGeometry = -> [Pad157]
  FullyConstrained = true
  MakeInternals = false
  MapMode = 5
  Placement = pos=(0,0,-4) rot=(1,0,0;3.14159rad)
  sketch-geometry (2):
    g0: Circle CenterX=7.15 CenterY=0 CenterZ=0 NormalX=0 NormalY=0 NormalZ=1 AngleXU=0 Radius=0.75
    g1: Circle CenterX=26.05 CenterY=0 CenterZ=0 NormalX=0 NormalY=0 NormalZ=1 AngleXU=0 Radius=0.75
  constraints (4):
    c: Coincident(g0,g-3)
    c: Coincident(g1,g-4)
    c: Radius(g0) = 0.75
    c: Radius(g1) = 0.75
FEATURE [PartDesign::Pocket] Pocket113
  BaseFeature = -> Pad157
  Direction = (0,0,1)
  Length = 4
  Length2 = 5
  Profile = -> Sketch245
  ReferenceAxis = -> Sketch245 [N_Axis]
  Refine = true
  Suppressed = false
  Type = 0
FEATURE [Sketcher::SketchObject] Sketch246
  ArcFitTolerance = 1e-06
  AttachmentSupport = -> [Pocket113]
  ExternalGeometry = -> [Pocket113]
  FullyConstrained = true
  MakeInternals = false
  MapMode = 5
  Placement = pos=(0,0,0) rot=(1,0,0;3.14159rad)
  sketch-geometry (1):
    g0: Circle CenterX=15.9183 CenterY=-5.2423 CenterZ=0 NormalX=0 NormalY=0 NormalZ=1 AngleXU=0 Radius=0.75
  constraints (4):
    c: Diameter(g0) = 1.5
    c: Tangent(g0,g-3)
    c: DistanceX(g-4,g0) = 1.4
    c: DistanceX(g0,g-5) = 1.3997
FEATURE [PartDesign::Pad] Pad158
  BaseFeature = -> Pocket113
  Direction = (0,0,-1)
  Length = 3.8
  Length2 = 10
  Profile = -> Sketch246
  ReferenceAxis = -> Sketch246 [N_Axis]
  Refine = true
  Suppressed = false
  Type = 0
FEATURE [Sketcher::SketchObject] Sketch247
  ArcFitTolerance = 1e-06
  AttachmentSupport = -> [Pad158]
  ExternalGeometry = -> [Pad158]
  FullyConstrained = true
  MakeInternals = false
  MapMode = 5
  Placement = pos=(0,0,0) rot=(1,0,0;3.14159rad)
  sketch-geometry (8):
    g0: LineSegment StartX=-3.15 StartY=1.65 StartZ=0 EndX=-3.15 EndY=-1.65 EndZ=0
    g1: LineSegment StartX=-3.15 StartY=-1.65 StartZ=0 EndX=3.15 EndY=-1.65 EndZ=0
    g2: LineSegment StartX=3.15 StartY=-1.65 StartZ=0 EndX=3.15 EndY=1.65 EndZ=0
    g3: LineSegment StartX=3.15 StartY=1.65 StartZ=0 EndX=-3.15 EndY=1.65 EndZ=0
    g4: LineSegment StartX=-3.85 StartY=2.35 StartZ=0 EndX=-3.85 EndY=-2.35 EndZ=0
    g5: LineSegment StartX=-3.85 StartY=-2.35 StartZ=0 EndX=3.85 EndY=-2.35 EndZ=0
    g6: LineSegment StartX=3.85 StartY=-2.35 StartZ=0 EndX=3.85 EndY=2.35 EndZ=0
    g7: LineSegment StartX=3.85 StartY=2.35 StartZ=0 EndX=-3.85 EndY=2.35 EndZ=0
  constraints (22):
    c: Coincident(g0,g1)
    c: Coincident(g1,g2)
    c: Coincident(g2,g3)
    c: Coincident(g3,g0)
    c: Vertical(g0)
    c: Vertical(g2)
    c: Horizontal(g1)
    c: Horizontal(g3)
    c: Coincident(g0,g-6)
    c: Coincident(g1,g-5)
    c: Coincident(g4,g5)
    c: Coincident(g5,g6)
    c: Coincident(g6,g7)
    c: Coincident(g7,g4)
    c: Vertical(g4)
    c: Vertical(g6)
    c: Horizontal(g5)
    c: Horizontal(g7)
    c: DistanceX(g2,g6) = 0.7
    c: DistanceX(g4,g0) = 0.7
    c: DistanceY(g5,g1) = 0.7
    c: DistanceY(g2,g6) = 0.7
FEATURE [PartDesign::Pad] Pad159
  BaseFeature = -> Pad158
  Direction = (0,0,-1)
  Length = 0.5
  Length2 = 10
  Profile = -> Sketch247
  ReferenceAxis = -> Sketch247 [N_Axis]
  Refine = true
  Suppressed = false
  Type = 0
FEATURE [Sketcher::SketchObject] Sketch248
  ArcFitTolerance = 1e-06
  AttachmentSupport = -> [Pad159]
  ExternalGeometry = -> [Pad159]
  FullyConstrained = true
  MakeInternals = false
  MapMode = 5
  Placement = pos=(0,0,-0.5) rot=(1,0,0;3.14159rad)
  sketch-geometry (8):
    g0: LineSegment StartX=-1 StartY=2.35 StartZ=0 EndX=-1 EndY=1.65 EndZ=0
    g1: LineSegment StartX=-1 StartY=1.65 StartZ=0 EndX=1 EndY=1.65 EndZ=0
    g2: LineSegment StartX=1 StartY=1.65 StartZ=0 EndX=1 EndY=2.35 EndZ=0
    g3: LineSegment StartX=1 StartY=2.35 StartZ=0 EndX=-1 EndY=2.35 EndZ=0
    g4: LineSegment StartX=-1 StartY=-1.65 StartZ=0 EndX=-1 EndY=-2.35 EndZ=0
    g5: LineSegment StartX=-1 StartY=-2.35 StartZ=0 EndX=1 EndY=-2.35 EndZ=0
    g6: LineSegment StartX=1 StartY=-2.35 StartZ=0 EndX=1 EndY=-1.65 EndZ=0
    g7: LineSegment StartX=1 StartY=-1.65 StartZ=0 EndX=-1 EndY=-1.65 EndZ=0
  constraints (24):
    c: Coincident(g0,g1)
    c: Coincident(g1,g2)
    c: Coincident(g2,g3)
    c: Coincident(g3,g0)
    c: Vertical(g0)
    c: Vertical(g2)
    c: Horizontal(g1)
    c: Horizontal(g3)
    c: PointOnObject(g0,g-3)
    c: PointOnObject(g1,g-4)
    c: Coincident(g4,g5)
    c: Coincident(g5,g6)
    c: Coincident(g6,g7)
    c: Coincident(g7,g4)
    c: Vertical(g4)
    c: Vertical(g6)
    c: Horizontal(g5)
    c: Horizontal(g7)
    c: PointOnObject(g4,g-5)
    c: PointOnObject(g5,g-6)
    c: DistanceX(g0,g-1) = 1
    c: DistanceX(g-1,g1) = 1
    c: DistanceX(g4,g-1) = 1
    c: DistanceX(g-1,g6) = 1
FEATURE [PartDesign::Pad] Pad160
  BaseFeature = -> Pad159
  Direction = (0,0,-1)
  Length = 0.1
  Length2 = 10
  Profile = -> Sketch248
  ReferenceAxis = -> Sketch248 [N_Axis]
  Refine = true
  Suppressed = false
  Type = 0
FEATURE [PartDesign::Body] Body015  label="Left_Inner_Leg"
  AllowCompound = false
  Group = -> [Sketch238,Pad153,Sketch239,Pocket110,Sketch240,Pad154,Sketch241,Pad155,Sketch242,Pad156,Sketch243,Pocket111,Sketch244,Pocket112,Pad157,Sketch245,Pocket113,Sketch246,Pad158,Sketch247,Pad159,Sketch248,Pad160]
  Origin = -> Origin016
  Placement = pos=(53.7,-27.4,-19.5) rot=(0,-0.71,-0.71;3.14159rad)
  Tip = -> Pad160
COMPONENT P11 — recipe-attached ("Pre_Right_Outer_Leg", modeled in this document).
Construction recipe (the document's own serialized feature program — sketch geometry with constraints, then the solid features built on it; lengths are millimeters unless a unit is written):

FEATURE [PartDesign::SubShapeBinder] Binder008
  BindCopyOnChange = 0
  BindMode = 2
  ClaimChildren = false
  Context = -> Body016 [Binder008.]
  Fuse = false
  MakeFace = true
  OffsetFill = false
  OffsetIntersection = false
  OffsetJoinType = 0
  OffsetOpenResult = false
  PartialLoad = false
  Refine = true
  Relative = true
  _Version = 2
FEATURE [PartDesign::Pad] Pad161
  Direction = (0,0,-1)
  Length = 4
  Length2 = 10
  Profile = -> Binder008
  Refine = true
  Suppressed = false
  Type = 0
FEATURE [Sketcher::SketchObject] Sketch249
  ArcFitTolerance = 1e-06
  AttachmentSupport = -> [Pad161]
  ExternalGeometry = -> [Pad161]
  FullyConstrained = true
  MakeInternals = false
  MapMode = 5
  Placement = pos=(0,0,-6.5) rot=(1,0,0;3.14159rad)
  sketch-geometry (8):
    g0: ArcOfCircle CenterX=18.5272 CenterY=169 CenterZ=0 NormalX=0 NormalY=0 NormalZ=1 AngleXU=0 Radius=175.012 StartAngle=4.78945 EndAngle=4.79805
    g1: LineSegment StartX=32 StartY=5 StartZ=0 EndX=32 EndY=1.5 EndZ=0
    g2: LineSegment StartX=32 StartY=1.5 StartZ=0 EndX=33.5 EndY=1.5 EndZ=0
    g3: LineSegment StartX=33.5 StartY=1.5 StartZ=0 EndX=33.5 EndY=5 EndZ=0
    g4: LineSegment StartX=33.5 StartY=5 StartZ=0 EndX=32 EndY=5 EndZ=0
    g5: LineSegment StartX=32 StartY=-5.49248 StartZ=0 EndX=32 EndY=-1.5 EndZ=0
    g6: LineSegment StartX=32 StartY=-1.5 StartZ=0 EndX=33.5 EndY=-1.5 EndZ=0
    g7: LineSegment StartX=33.5 StartY=-1.5 StartZ=0 EndX=33.5 EndY=-5.37017 EndZ=0
  constraints (20):
    c: Radius(g-3) = 175.012
    c: Coincident(g0,g-8)
    c: PointOnObject(g0,g-9)
    c: Coincident(g0,g-3)
    c: Coincident(g1,g2)
    c: Coincident(g2,g3)
    c: Coincident(g3,g4)
    c: Coincident(g4,g1)
    c: Vertical(g1)
    c: Vertical(g3)
    c: Horizontal(g2)
    c: Horizontal(g4)
    c: Coincident(g1,g-4)
    c: Coincident(g2,g-6)
    c: Coincident(g5,g0)
    c: Coincident(g5,g-8)
    c: Coincident(g6,g5)
    c: Coincident(g6,g-9)
    c: Coincident(g7,g6)
    c: Coincident(g7,g0)
FEATURE [PartDesign::Pocket] Pocket114
  BaseFeature = -> Pad161
  Direction = (0,0,1)
  Length = 0.5
  Length2 = 5
  Profile = -> Sketch249
  ReferenceAxis = -> Sketch249 [N_Axis]
  Refine = true
  Suppressed = false
  Type = 0
FEATURE [Sketcher::SketchObject] Sketch250
  ArcFitTolerance = 1e-06
  AttachmentSupport = -> [Pocket114]
  ExternalGeometry = -> [Pocket114]
  FullyConstrained = true
  MakeInternals = false
  MapMode = 5
  Placement = pos=(0,0,-6) rot=(1,0,0;3.14159rad)
  sketch-geometry (4):
    g0: ArcOfCircle CenterX=0 CenterY=3e-16 CenterZ=0 NormalX=0 NormalY=0 NormalZ=1 AngleXU=0 Radius=5 StartAngle=1.5708 EndAngle=4.61995
    g1: ArcOfCircle CenterX=18.5272 CenterY=169 CenterZ=0 NormalX=0 NormalY=0 NormalZ=1 AngleXU=0 Radius=175.012 StartAngle=4.60368 EndAngle=4.78945
    g2: LineSegment StartX=32 StartY=-5.49248 StartZ=0 EndX=32 EndY=5 EndZ=0
    g3: LineSegment StartX=32 StartY=5 StartZ=0 EndX=0 EndY=5 EndZ=0
  constraints (9):
    c: Tangent(g0,g-7) = -1.5708
    c: Coincident(g0,g-7)
    c: Coincident(g1,g0)
    c: Coincident(g1,g-4)
    c: Tangent(g1,g-3)
    c: Coincident(g2,g1)
    c: Coincident(g2,g-5)
    c: Coincident(g3,g2)
    c: Coincident(g3,g0)
FEATURE [PartDesign::Pad] Pad162
  BaseFeature = -> Pocket114
  Direction = (0,0,-1)
  Length = 1
  Length2 = 10
  Profile = -> Sketch250
  ReferenceAxis = -> Sketch250 [N_Axis]
  Refine = true
  Reversed = true
  Suppressed = false
  Type = 0
FEATURE [Sketcher::SketchObject] Sketch251
  ArcFitTolerance = 1e-06
  AttachmentSupport = -> [Pad162]
  ExternalGeometry = -> [Pad162]
  FullyConstrained = true
  MakeInternals = false
  MapMode = 5
  Placement = pos=(33.5,7.933e-13,0) rot=(0.57735,0.57735,0.57735;2.0944rad)
  sketch-geometry (6):
    g0: ArcOfCircle CenterX=-8.307e-13 CenterY=-2.5 CenterZ=0 NormalX=0 NormalY=0 NormalZ=1 AngleXU=0 Radius=1.5 StartAngle=3.14159 EndAngle=6.28319
    g1: LineSegment [constr] StartX=-1.5 StartY=-2.5 StartZ=0 EndX=-8.307e-13 EndY=-2.5 EndZ=0
    g2: LineSegment [constr] StartX=-8.307e-13 StartY=-2.5 StartZ=0 EndX=1.5 EndY=-2.5 EndZ=0
    g3: LineSegment StartX=-1.5 StartY=-2.5 StartZ=0 EndX=-1.5 EndY=-6 EndZ=0
    g4: LineSegment StartX=-1.5 StartY=-6 StartZ=0 EndX=1.5 EndY=-6 EndZ=0
    g5: LineSegment StartX=1.5 StartY=-6 StartZ=0 EndX=1.5 EndY=-2.5 EndZ=0
  constraints (13):
    c: Coincident(g0,g-4)
    c: Coincident(g0,g-3)
    c: Coincident(g1,g0)
    c: Coincident(g1,g0)
    c: Coincident(g2,g0)
    c: Coincident(g2,g0)
    c: Angle(g2,g1) = 3.14159
    c: Coincident(g3,g0)
    c: Coincident(g3,g-4)
    c: Coincident(g4,g3)
    c: Coincident(g4,g-3)
    c: Coincident(g5,g4)
    c: Coincident(g5,g0)
FEATURE [PartDesign::Pad] Pad163
  BaseFeature = -> Pad162
  Direction = (1,2.36e-14,1e-16)
  Length = 1.5
  Length2 = 10
  Profile = -> Sketch251
  ReferenceAxis = -> Sketch251 [N_Axis]
  Refine = true
  Reversed = true
  Suppressed = false
  Type = 0
FEATURE [Sketcher::SketchObject] Sketch252
  ArcFitTolerance = 1e-06
  AttachmentSupport = -> [Pad163]
  ExternalGeometry = -> [Pad163]
  FullyConstrained = true
  MakeInternals = false
  MapMode = 5
  Placement = pos=(0,0,-6) rot=(1,0,0;3.14159rad)
  sketch-geometry (4):
    g0: ArcOfCircle CenterX=0 CenterY=0 CenterZ=0 NormalX=0 NormalY=0 NormalZ=1 AngleXU=0 Radius=4.85 StartAngle=0.748325 EndAngle=5.72466
    g1: LineSegment StartX=3.55422 StartY=3.3 StartZ=0 EndX=33.5 EndY=3.3 EndZ=0
    g2: LineSegment StartX=4.11299 StartY=-2.57017 StartZ=0 EndX=33.5 EndY=-2.57017 EndZ=0
    g3: LineSegment StartX=33.5 StartY=-2.57017 StartZ=0 EndX=33.5 EndY=3.3 EndZ=0
  constraints (13):
    c: Diameter(g0) = 9.7
    c: Coincident(g0,g-1)
    c: Coincident(g1,g0)
    c: PointOnObject(g1,g-5)
    c: Horizontal(g1)
    c: Coincident(g2,g0)
    c: PointOnObject(g2,g-5)
    c: Horizontal(g2)
    c: Coincident(g3,g2)
    c: Coincident(g3,g1)
    c: DistanceY(g1,g-5) = 1.7
    c: DistanceY(g-5,g2) = 2.8
    c: DistanceY(g2,g1) = 5.87017
FEATURE [PartDesign::Pad] Pad164
  BaseFeature = -> Pad163
  Direction = (0,0,-1)
  Length = 0.5
  Length2 = 10
  Profile = -> Sketch252
  ReferenceAxis = -> Sketch252 [N_Axis]
  Refine = true
  Suppressed = false
  Type = 0
FEATURE [Sketcher::SketchObject] Sketch253
  ArcFitTolerance = 1e-06
  AttachmentSupport = -> [Pad164]
  ExternalGeometry = -> [Pad164]
  FullyConstrained = true
  MakeInternals = false
  MapMode = 5
  Placement = pos=(0,0,-6.5) rot=(1,0,0;3.14159rad)
  sketch-geometry (2):
    g0: Circle CenterX=0 CenterY=0 CenterZ=0 NormalX=0 NormalY=0 NormalZ=1 AngleXU=0 Radius=3.8
    g1: Circle CenterX=0 CenterY=0 CenterZ=0 NormalX=0 NormalY=0 NormalZ=1 AngleXU=0 Radius=2
  constraints (4):
    c: Coincident(g0,g-1)
    c: Coincident(g1,g0)
    c: Diameter(g0) = 7.6
    c: Diameter(g1) = 4
FEATURE [PartDesign::Pad] Pad165
  BaseFeature = -> Pad164
  Direction = (0,0,-1)
  Length = 1
  Length2 = 10
  Profile = -> Sketch253
  ReferenceAxis = -> Sketch253 [N_Axis]
  Refine = true
  Suppressed = false
  Type = 0
FEATURE [Sketcher::SketchObject] Sketch254
  ArcFitTolerance = 1e-06
  AttachmentSupport = -> [Pad165]
  ExternalGeometry = -> [Pad165]
  FullyConstrained = true
  MakeInternals = false
  MapMode = 5
  Placement = pos=(0,0,-6.5) rot=(1,0,0;3.14159rad)
  sketch-geometry (4):
    g0: LineSegment StartX=33.5 StartY=3.3 StartZ=0 EndX=5 EndY=3.3 EndZ=0
    g1: LineSegment StartX=5 StartY=3.3 StartZ=0 EndX=5 EndY=-2.57017 EndZ=0
    g2: LineSegment StartX=5 StartY=-2.57017 StartZ=0 EndX=33.5 EndY=-2.57017 EndZ=0
    g3: LineSegment StartX=33.5 StartY=-2.57017 StartZ=0 EndX=33.5 EndY=3.3 EndZ=0
  constraints (11):
    c: Coincident(g0,g1)
    c: Coincident(g1,g2)
    c: Coincident(g2,g3)
    c: Coincident(g3,g0)
    c: Horizontal(g0)
    c: Horizontal(g2)
    c: Vertical(g1)
    c: Vertical(g3)
    c: Coincident(g0,g-4)
    c: PointOnObject(g1,g-5)
    c: DistanceX(g0,g0) = 28.5
FEATURE [PartDesign::Pad] Pad166
  BaseFeature = -> Pad165
  Direction = (0,0,-1)
  Length = 0.5
  Length2 = 10
  Profile = -> Sketch254
  ReferenceAxis = -> Sketch254 [N_Axis]
  Refine = true
  Suppressed = false
  Type = 0
FEATURE [Sketcher::SketchObject] Sketch255
  ArcFitTolerance = 1e-06
  AttachmentSupport = -> [Pad166]
  ExternalGeometry = -> [Pad166]
  FullyConstrained = true
  MakeInternals = false
  MapMode = 5
  Placement = pos=(0,0,-7) rot=(1,0,0;3.14159rad)
  sketch-geometry (5):
    g0: Circle CenterX=7.15 CenterY=0 CenterZ=0 NormalX=0 NormalY=0 NormalZ=1 AngleXU=0 Radius=2.25
    g1: Circle CenterX=26.05 CenterY=0 CenterZ=0 NormalX=0 NormalY=0 NormalZ=1 AngleXU=0 Radius=2.25
    g2: LineSegment [constr] StartX=26.05 StartY=0 StartZ=0 EndX=28.3 EndY=0 EndZ=0
    g3: LineSegment [constr] StartX=26.05 StartY=0 StartZ=0 EndX=23.8 EndY=0 EndZ=0
    g4: LineSegment [constr] StartX=7.15 StartY=0 StartZ=0 EndX=9.4 EndY=0 EndZ=0
  constraints (15):
    c: PointOnObject(g0,g-1)
    c: PointOnObject(g1,g-1)
    c: Diameter(g0) = 4.5
    c: Diameter(g1) = 4.5
    c: Coincident(g2,g1)
    c: PointOnObject(g2,g1)
    c: Horizontal(g2)
    c: DistanceX(g2,g-4) = 5.2
    c: Coincident(g3,g1)
    c: PointOnObject(g3,g1)
    c: Horizontal(g3)
    c: Coincident(g4,g0)
    c: PointOnObject(g4,g0)
    c: Horizontal(g4)
    c: DistanceX(g4,g3) = 14.4
FEATURE [Sketcher::SketchObject] Sketch256
  ArcFitTolerance = 1e-06
  AttachmentSupport = -> [Pad166]
  ExternalGeometry = -> [Pad166]
  FullyConstrained = true
  MakeInternals = false
  MapMode = 5
  Placement = pos=(0,0,-5) rot=(0,0,1;0rad)
  sketch-geometry (4):
    g0: LineSegment StartX=32 StartY=1.95 StartZ=0 EndX=-4.60407 EndY=1.95 EndZ=0
    g1: LineSegment StartX=-4.60407 StartY=1.95 StartZ=0 EndX=-4.60407 EndY=-1.95 EndZ=0
    g2: LineSegment StartX=-4.60407 StartY=-1.95 StartZ=0 EndX=32 EndY=-1.95 EndZ=0
    g3: LineSegment StartX=32 StartY=-1.95 StartZ=0 EndX=32 EndY=1.95 EndZ=0
  constraints (12):
    c: Coincident(g0,g1)
    c: Coincident(g1,g2)
    c: Coincident(g2,g3)
    c: Coincident(g3,g0)
    c: Horizontal(g0)
    c: Horizontal(g2)
    c: Vertical(g1)
    c: Vertical(g3)
    c: PointOnObject(g0,g-3)
    c: DistanceY(g3,g3) = 3.9
    c: DistanceY(g1,g-1) = 1.95
    c: PointOnObject(g0,g-4)
FEATURE [PartDesign::Pocket] Pocket115
  BaseFeature = -> Pad166
  Direction = (0,0,-1)
  Length = 1
  Length2 = 5
  Profile = -> Sketch256
  ReferenceAxis = -> Sketch256 [N_Axis]
  Refine = true
  Suppressed = false
  Type = 0
FEATURE [Sketcher::SketchObject] Sketch257
  ArcFitTolerance = 1e-06
  AttachmentSupport = -> [Pocket115]
  ExternalGeometry = -> [Sketch255]
  FullyConstrained = true
  MakeInternals = false
  MapMode = 5
  Placement = pos=(0,0,-6) rot=(0,0,1;0rad)
  sketch-geometry (2):
    g0: Circle CenterX=7.15 CenterY=0 CenterZ=0 NormalX=0 NormalY=0 NormalZ=1 AngleXU=0 Radius=3.5
    g1: Circle CenterX=26.05 CenterY=0 CenterZ=0 NormalX=0 NormalY=0 NormalZ=1 AngleXU=0 Radius=3.5
  constraints (4):
    c: Coincident(g0,g-3)
    c: Coincident(g1,g-4)
    c: Diameter(g0) = 7
    c: Diameter(g1) = 7
FEATURE [PartDesign::Pad] Pad167
  BaseFeature = -> Pocket115
  Direction = (0,0,1)
  Length = 2.8
  Length2 = 10
  Profile = -> Sketch257
  ReferenceAxis = -> Sketch257 [N_Axis]
  Refine = true
  Suppressed = false
  Type = 0
FEATURE [Sketcher::SketchObject] Sketch258
  ArcFitTolerance = 1e-06
  AttachmentSupport = -> [Pad167]
  ExternalGeometry = -> [Pad167]
  FullyConstrained = true
  MakeInternals = false
  MapMode = 5
  Placement = pos=(0,0,-3.2) rot=(0,0,1;0rad)
  sketch-geometry (2):
    g0: Circle CenterX=7.15 CenterY=0 CenterZ=0 NormalX=0 NormalY=0 NormalZ=1 AngleXU=0 Radius=2.45
    g1: Circle CenterX=26.05 CenterY=0 CenterZ=0 NormalX=0 NormalY=0 NormalZ=1 AngleXU=0 Radius=2.45
  constraints (4):
    c: Coincident(g0,g-3)
    c: Coincident(g1,g-4)
    c: Diameter(g0) = 4.9
    c: Diameter(g1) = 4.9
FEATURE [PartDesign::Pocket] Pocket116
  BaseFeature = -> Pad167
  Direction = (0,0,-1)
  Length = 1
  Length2 = 5
  Profile = -> Sketch258
  ReferenceAxis = -> Sketch258 [N_Axis]
  Refine = true
  Suppressed = false
  Type = 0
FEATURE [PartDesign::Pocket] Pocket117
  BaseFeature = -> Pocket116
  Direction = (0,0,1)
  Length = 2
  Length2 = 5
  Profile = -> Sketch255
  ReferenceAxis = -> Sketch255 [N_Axis]
  Refine = true
  Suppressed = false
  Type = 0
FEATURE [Sketcher::SketchObject] Sketch259
  ArcFitTolerance = 1e-06
  AttachmentSupport = -> [Pocket117]
  ExternalGeometry = -> [Pocket117]
  FullyConstrained = true
  MakeInternals = false
  MapMode = 5
  Placement = pos=(0,0,-5) rot=(1,0,0;3.14159rad)
  sketch-geometry (2):
    g0: Circle CenterX=7.15 CenterY=0 CenterZ=0 NormalX=0 NormalY=0 NormalZ=1 AngleXU=0 Radius=1
    g1: Circle CenterX=26.05 CenterY=0 CenterZ=0 NormalX=0 NormalY=0 NormalZ=1 AngleXU=0 Radius=1
  constraints (4):
    c: Coincident(g0,g-3)
    c: Coincident(g1,g-4)
    c: Radius(g0) = 1
    c: Radius(g1) = 1
FEATURE [PartDesign::Pocket] Pocket118
  BaseFeature = -> Pocket117
  Direction = (0,0,1)
  Length = 5
  Length2 = 5
  Profile = -> Sketch259
  ReferenceAxis = -> Sketch259 [N_Axis]
  Refine = true
  Suppressed = false
  Type = 0
FEATURE [Sketcher::SketchObject] Sketch260
  ArcFitTolerance = 1e-06
  AttachmentSupport = -> [Pocket118]
  FullyConstrained = true
  MakeInternals = false
  MapMode = 5
  Placement = pos=(0,0,-6) rot=(0,0,1;0rad)
  sketch-geometry (9):
    g0: LineSegment StartX=-3.1 StartY=2.45 StartZ=0 EndX=-3.1 EndY=-2.45 EndZ=0
    g1: LineSegment StartX=-3.1 StartY=-2.45 StartZ=0 EndX=-1.6 EndY=-2.45 EndZ=0
    g2: LineSegment StartX=-1.6 StartY=-2.45 StartZ=0 EndX=-1.6 EndY=2.45 EndZ=0
    g3: LineSegment StartX=-1.6 StartY=2.45 StartZ=0 EndX=-3.1 EndY=2.45 EndZ=0
    g4: LineSegment StartX=1.6 StartY=2.45 StartZ=0 EndX=1.6 EndY=-2.45 EndZ=0
    g5: LineSegment StartX=1.6 StartY=-2.45 StartZ=0 EndX=3.1 EndY=-2.45 EndZ=0
    g6: LineSegment StartX=3.1 StartY=-2.45 StartZ=0 EndX=3.1 EndY=2.45 EndZ=0
    g7: LineSegment StartX=3.1 StartY=2.45 StartZ=0 EndX=1.6 EndY=2.45 EndZ=0
    g8: LineSegment [constr] StartX=1.6 StartY=-2.45 StartZ=0 EndX=-1.6 EndY=-2.45 EndZ=0
  constraints (26):
    c: Coincident(g0,g1)
    c: Coincident(g1,g2)
    c: Coincident(g2,g3)
    c: Coincident(g3,g0)
    c: Vertical(g0)
    c: Vertical(g2)
    c: Horizontal(g1)
    c: Horizontal(g3)
    c: Coincident(g4,g5)
    c: Coincident(g5,g6)
    c: Coincident(g6,g7)
    c: Coincident(g7,g4)
    c: Vertical(g4)
    c: Vertical(g6)
    c: Horizontal(g5)
    c: Horizontal(g7)
    c: DistanceX(g4,g6) = 1.5
    c: DistanceX(g0,g2) = 1.5
    c: DistanceX(g2,g4) = 3.2
    c: DistanceY(g0,g0) = 4.9
    c: DistanceY(g4,g4) = 4.9
    c: DistanceY(g4,g-1) = 2.45
    c: Coincident(g8,g4)
    c: Coincident(g8,g1)
    c: Horizontal(g8)
    c: DistanceX(g2,g-1) = 1.6
FEATURE [PartDesign::Pad] Pad168
  BaseFeature = -> Pocket118
  Direction = (0,0,1)
  Length = 5.4
  Length2 = 10
  Profile = -> Sketch260
  ReferenceAxis = -> Sketch260 [N_Axis]
  Refine = true
  Suppressed = false
  Type = 0
FEATURE [Sketcher::SketchObject] Sketch261
  ArcFitTolerance = 1e-06
  AttachmentSupport = -> [Pad168]
  ExternalGeometry = -> [Pad168]
  FullyConstrained = true
  MakeInternals = false
  MapMode = 5
  Placement = pos=(0,0,-0.6) rot=(0,0,1;0rad)
  sketch-geometry (8):
    g0: LineSegment StartX=-3.1 StartY=1.6 StartZ=0 EndX=-3.1 EndY=-1.6 EndZ=0
    g1: LineSegment StartX=-3.1 StartY=-1.6 StartZ=0 EndX=-1.6 EndY=-1.6 EndZ=0
    g2: LineSegment StartX=-1.6 StartY=-1.6 StartZ=0 EndX=-1.6 EndY=1.6 EndZ=0
    g3: LineSegment StartX=-1.6 StartY=1.6 StartZ=0 EndX=-3.1 EndY=1.6 EndZ=0
    g4: LineSegment StartX=1.6 StartY=1.6 StartZ=0 EndX=1.6 EndY=-1.6 EndZ=0
    g5: LineSegment StartX=1.6 StartY=-1.6 StartZ=0 EndX=3.1 EndY=-1.6 EndZ=0
    g6: LineSegment StartX=3.1 StartY=-1.6 StartZ=0 EndX=3.1 EndY=1.6 EndZ=0
    g7: LineSegment StartX=3.1 StartY=1.6 StartZ=0 EndX=1.6 EndY=1.6 EndZ=0
  constraints (24):
    c: Coincident(g0,g1)
    c: Coincident(g1,g2)
    c: Coincident(g2,g3)
    c: Coincident(g3,g0)
    c: Vertical(g0)
    c: Vertical(g2)
    c: Horizontal(g1)
    c: Horizontal(g3)
    c: PointOnObject(g0,g-3)
    c: PointOnObject(g1,g-4)
    c: Coincident(g4,g5)
    c: Coincident(g5,g6)
    c: Coincident(g6,g7)
    c: Coincident(g7,g4)
    c: Vertical(g4)
    c: Vertical(g6)
    c: Horizontal(g5)
    c: Horizontal(g7)
    c: PointOnObject(g4,g-5)
    c: PointOnObject(g5,g-6)
    c: DistanceY(g0,g0) = 3.2
    c: DistanceY(g4,g4) = 3.2
    c: DistanceY(g-1,g4) = 1.6
    c: DistanceY(g-1,g2) = 1.6
FEATURE [PartDesign::Pad] Pad169
  BaseFeature = -> Pad168
  Direction = (0,0,1)
  Length = 2
  Length2 = 10
  Profile = -> Sketch261
  ReferenceAxis = -> Sketch261 [N_Axis]
  Refine = true
  Suppressed = false
  Type = 0
FEATURE [Sketcher::SketchObject] Sketch262
  ArcFitTolerance = 1e-06
  AttachmentSupport = -> [Pad169]
  ExternalGeometry = -> [Pad169]
  FullyConstrained = true
  MakeInternals = false
  MapMode = 5
  Placement = pos=(0,1.4e-15,-6) rot=(1,0,0;3.14159rad)
  sketch-geometry (15):
    g0: ArcOfCircle CenterX=10.6 CenterY=1.97712 CenterZ=0 NormalX=0 NormalY=0 NormalZ=1 AngleXU=0 Radius=2 StartAngle=0.722734 EndAngle=2.41886
    g1: ArcOfCircle CenterX=15.1 CenterY=1.97712 CenterZ=0 NormalX=0 NormalY=0 NormalZ=1 AngleXU=0 Radius=2 StartAngle=0.722734 EndAngle=2.41886
    g2: ArcOfCircle CenterX=19.6 CenterY=1.97712 CenterZ=0 NormalX=0 NormalY=0 NormalZ=1 AngleXU=0 Radius=2 StartAngle=0.722734 EndAngle=2.41886
    g3: ArcOfCircle CenterX=24.1 CenterY=1.97712 CenterZ=0 NormalX=0 NormalY=0 NormalZ=1 AngleXU=0 Radius=2 StartAngle=0.722734 EndAngle=2.41886
    g4: ArcOfCircle CenterX=28.6 CenterY=1.97712 CenterZ=0 NormalX=0 NormalY=0 NormalZ=1 AngleXU=0 Radius=2 StartAngle=0.722734 EndAngle=2.41886
    g5: ArcOfCircle CenterX=14 CenterY=-3.53842 CenterZ=0 NormalX=0 NormalY=0 NormalZ=1 AngleXU=0 Radius=2 StartAngle=2.63623 EndAngle=6.78855
    g6: ArcOfCircle CenterX=23.5 CenterY=-3.53842 CenterZ=0 NormalX=0 NormalY=0 NormalZ=1 AngleXU=0 Radius=2 StartAngle=2.63623 EndAngle=6.78855
    g7: LineSegment [constr] StartX=23.5 StartY=-3.53842 StartZ=0 EndX=25.5 EndY=-3.53842 EndZ=0
    g8: LineSegment StartX=9.1 StartY=3.3 StartZ=0 EndX=12.1 EndY=3.3 EndZ=0
    g9: LineSegment StartX=13.6 StartY=3.3 StartZ=0 EndX=16.6 EndY=3.3 EndZ=0
    g10: LineSegment StartX=18.1 StartY=3.3 StartZ=0 EndX=21.1 EndY=3.3 EndZ=0
    g11: LineSegment StartX=22.6 StartY=3.3 StartZ=0 EndX=25.6 EndY=3.3 EndZ=0
    g12: LineSegment StartX=27.1 StartY=3.3 StartZ=0 EndX=30.1 EndY=3.3 EndZ=0
    g13: LineSegment StartX=25.25 StartY=-2.57017 StartZ=0 EndX=21.75 EndY=-2.57017 EndZ=0
    g14: LineSegment StartX=15.75 StartY=-2.57017 StartZ=0 EndX=12.25 EndY=-2.57017 EndZ=0
  constraints (52):
    c: PointOnObject(g0,g-3)
    c: PointOnObject(g0,g-3)
    c: PointOnObject(g1,g-3)
    c: PointOnObject(g1,g-3)
    c: PointOnObject(g2,g-3)
    c: PointOnObject(g2,g-3)
    c: PointOnObject(g3,g-3)
    c: PointOnObject(g4,g-3)
    c: PointOnObject(g4,g-3)
    c: PointOnObject(g5,g-4)
    c: PointOnObject(g5,g-4)
    c: PointOnObject(g6,g-4)
    c: PointOnObject(g6,g-4)
    c: Diameter(g1) = 4
    c: DistanceX(g1,g1) = 3
    c: Diameter(g0) = 4
    c: Diameter(g2) = 4
    c: Diameter(g3) = 4
    c: Diameter(g4) = 4
    c: Diameter(g5) = 4
    c: Diameter(g6) = 4
    c: DistanceX(g0,g0) = 3
    c: DistanceX(g2,g2) = 3
    c: PointOnObject(g3,g-3)
    c: DistanceX(g3,g3) = 3
    c: DistanceX(g4,g4) = 3
    c: DistanceX(g5,g5) = 3.5
    c: DistanceX(g6,g6) = 3.5
    c: DistanceX(g5,g6) = 6
    c: DistanceX(g0,g1) = 1.5
    c: DistanceX(g1,g2) = 1.5
    c: DistanceX(g2,g3) = 1.5
    c: DistanceX(g3,g4) = 1.5
    c: Coincident(g7,g6)
    c: PointOnObject(g7,g6)
    c: Horizontal(g7)
    c: DistanceX(g7,g-5) = 8
    c: DistanceX(g4,g-6) = 3.4
    c: Coincident(g8,g0)
    c: Coincident(g8,g0)
    c: Coincident(g9,g1)
    c: Coincident(g9,g1)
    c: Coincident(g10,g2)
    c: Coincident(g10,g2)
    c: Coincident(g11,g3)
    c: Coincident(g11,g3)
    c: Coincident(g12,g4)
    c: Coincident(g12,g4)
    c: Coincident(g13,g6)
    c: Coincident(g13,g6)
    c: Coincident(g14,g5)
    c: Coincident(g14,g5)
FEATURE [PartDesign::Pad] Pad170
  BaseFeature = -> Pad169
  Direction = (0,0,-1)
  Length = 0.25
  Length2 = 10
  Profile = -> Pad169 [Face9]
  Refine = true
  Suppressed = false
  Type = 0
FEATURE [PartDesign::Pad] Pad171
  BaseFeature = -> Pad170
  Direction = (0,0,-1)
  Length = 0.75
  Length2 = 10
  Profile = -> Sketch262
  ReferenceAxis = -> Sketch262 [N_Axis]
  Refine = true
  Suppressed = false
  Type = 0
FEATURE [Sketcher::SketchObject] Sketch263
  ArcFitTolerance = 1e-06
  AttachmentSupport = -> [Pad171]
  ExternalGeometry = -> [Pad171]
  FullyConstrained = true
  MakeInternals = false
  MapMode = 5
  Placement = pos=(0,0,-6.75) rot=(1,0,0;3.14159rad)
  sketch-geometry (12):
    g0: LineSegment [constr] StartX=14 StartY=-3.53842 StartZ=0 EndX=12 EndY=-3.53842 EndZ=0
    g1: LineSegment [constr] StartX=14 StartY=-3.53842 StartZ=0 EndX=16 EndY=-3.53842 EndZ=0
    g2: LineSegment [constr] StartX=23.5 StartY=-3.53842 StartZ=0 EndX=21.5 EndY=-3.53842 EndZ=0
    g3: LineSegment [constr] StartX=23.5 StartY=-3.53842 StartZ=0 EndX=25.5 EndY=-3.53842 EndZ=0
    g4: LineSegment StartX=16 StartY=-3.53842 StartZ=0 EndX=12 EndY=-3.53842 EndZ=0
    g5: LineSegment StartX=16 StartY=-3.53842 StartZ=0 EndX=16 EndY=-2.57017 EndZ=0
    g6: LineSegment StartX=16 StartY=-2.57017 StartZ=0 EndX=12 EndY=-2.57017 EndZ=0
    g7: LineSegment StartX=12 StartY=-3.53842 StartZ=0 EndX=12 EndY=-2.57017 EndZ=0
    g8: LineSegment StartX=21.5 StartY=-3.53842 StartZ=0 EndX=25.5 EndY=-3.53842 EndZ=0
    g9: LineSegment StartX=21.5 StartY=-3.53842 StartZ=0 EndX=21.5 EndY=-2.57017 EndZ=0
    g10: LineSegment StartX=25.5 StartY=-3.53842 StartZ=0 EndX=25.5 EndY=-2.57017 EndZ=0
    g11: LineSegment StartX=25.5 StartY=-2.57017 StartZ=0 EndX=21.5 EndY=-2.57017 EndZ=0
  constraints (33):
    c: Coincident(g0,g-3)
    c: PointOnObject(g0,g-3)
    c: Horizontal(g0)
    c: Coincident(g1,g0)
    c: PointOnObject(g1,g-3)
    c: Horizontal(g1)
    c: Coincident(g2,g-4)
    c: PointOnObject(g2,g-4)
    c: Horizontal(g2)
    c: Coincident(g3,g2)
    c: PointOnObject(g3,g-4)
    c: Horizontal(g3)
    c: PointOnObject(g4,g-3)
    c: Horizontal(g4)
    c: Vertical(g5)
    c: Coincident(g6,g5)
    c: Horizontal(g6)
    c: Vertical(g7)
    c: Coincident(g7,g6)
    c: PointOnObject(g-5,g6)
    c: Coincident(g4,g0)
    c: Coincident(g7,g0)
    c: Coincident(g5,g4)
    c: Coincident(g8,g2)
    c: Coincident(g8,g3)
    c: Coincident(g9,g8)
    c: Coincident(g11,g10)
    c: Coincident(g11,g9)
    c: Horizontal(g11)
    c: PointOnObject(g-6,g11)
    c: Vertical(g9)
    c: Vertical(g10)
    c: Coincident(g10,g8)
FEATURE [PartDesign::Pad] Pad172
  BaseFeature = -> Pad171
  Direction = (0,0,-1)
  Length = 0.75
  Length2 = 10
  Profile = -> Sketch263
  ReferenceAxis = -> Sketch263 [N_Axis]
  Refine = true
  Reversed = true
  Suppressed = false
  Type = 0
FEATURE [PartDesign::Body] Body016  label="Left_Outer_Leg"
  AllowCompound = false
  Group = -> [Binder008,Pad161,Sketch249,Pocket114,Sketch250,Pad162,Sketch251,Pad163,Sketch252,Pad164,Sketch253,Pad165,Sketch254,Pad166,Sketch255,Sketch256,Pocket115,Sketch257,Pad167,Sketch258,Pocket116,Pocket117,Sketch259,Pocket118,Sketch260,Pad168,Sketch261,Pad169,Sketch262,Pad170,Pad171,Sketch263,Pad172]
  Origin = -> Origin017
  Placement = pos=(53.7,-27.4,-19.5) rot=(0,-0.71,-0.71;3.14159rad)
  Tip = -> Pad172
COMPONENT P12 — recipe-attached ("Pre_Right_Ankle", modeled in this document).
Construction recipe (the document's own serialized feature program — sketch geometry with constraints, then the solid features built on it; lengths are millimeters unless a unit is written):

FEATURE [PartDesign::SubShapeBinder] Binder009
  BindCopyOnChange = 0
  BindMode = 2
  ClaimChildren = false
  Context = -> Body017 [Binder009.]
  Fuse = false
  MakeFace = true
  OffsetFill = false
  OffsetIntersection = false
  OffsetJoinType = 0
  OffsetOpenResult = false
  PartialLoad = false
  Refine = true
  Relative = true
  _Version = 2
FEATURE [Sketcher::SketchObject] Sketch264
  ArcFitTolerance = 1e-06
  AttachmentSupport = -> [Binder009]
  ExternalGeometry = -> [Binder009]
  FullyConstrained = true
  MakeInternals = false
  MapMode = 5
  Placement = pos=(0,0,1.5) rot=(0,0,1;0rad)
  sketch-geometry (6):
    g0: ArcOfCircle CenterX=37 CenterY=0 CenterZ=0 NormalX=0 NormalY=0 NormalZ=1 AngleXU=0 Radius=6.5 StartAngle=4.71239 EndAngle=7.76154
    g1: LineSegment [constr] StartX=37 StartY=0 StartZ=0 EndX=37 EndY=-6.5 EndZ=0
    g2: LineSegment [constr] StartX=37 StartY=0 StartZ=0 EndX=43.5 EndY=0 EndZ=0
    g3: LineSegment StartX=37 StartY=-6.5 StartZ=0 EndX=33.5 EndY=-6.5 EndZ=0
    g4: LineSegment StartX=33.5 StartY=-6.5 StartZ=0 EndX=33.5 EndY=6.87 EndZ=0
    g5: ArcOfCircle CenterX=18.5075 CenterY=-169.002 CenterZ=0 NormalX=0 NormalY=0 NormalZ=1 AngleXU=0 Radius=176.51 StartAngle=1.46242 EndAngle=1.48576
  constraints (19):
    c: Diameter(g0) = 13
    c: Coincident(g1,g0)
    c: Coincident(g1,g0)
    c: Vertical(g1)
    c: Coincident(g2,g0)
    c: PointOnObject(g2,g0)
    c: Horizontal(g2)
    c: DistanceX(g-3,g2) = 10
    c: PointOnObject(g2,g-1)
    c: DistanceX(g0,g0) = 0.6
    c: Coincident(g3,g0)
    c: Horizontal(g3)
    c: Coincident(g4,g3)
    c: Vertical(g4)
    c: PointOnObject(g-3,g4)
    c: Coincident(g5,g0)
    c: Coincident(g5,g4)
    c: DistanceY(g3,g4) = 13.37
    c: Radius(g5) = 176.51
FEATURE [PartDesign::Pad] Pad173
  Direction = (0,0,1)
  Length = 8
  Length2 = 10
  Profile = -> Sketch264
  ReferenceAxis = -> Sketch264 [N_Axis]
  Refine = true
  Reversed = true
  Suppressed = false
  Type = 0
FEATURE [Sketcher::SketchObject] Sketch265
  ArcFitTolerance = 1e-06
  AttachmentSupport = -> [Pad173]
  ExternalGeometry = -> [Pad173]
  FullyConstrained = true
  MakeInternals = false
  MapMode = 5
  Placement = pos=(0,0,-6.5) rot=(1,0,0;3.14159rad)
  sketch-geometry (6):
    g0: LineSegment StartX=33.5 StartY=5 StartZ=0 EndX=33.5 EndY=-5.37 EndZ=0
    g1: LineSegment StartX=33.5 StartY=-5.37 StartZ=0 EndX=37.6 EndY=-4.96387 EndZ=0
    g2: LineSegment StartX=33.5 StartY=5 StartZ=0 EndX=37 EndY=5 EndZ=0
    g3: ArcOfCircle CenterX=37 CenterY=0 CenterZ=0 NormalX=0 NormalY=0 NormalZ=1 AngleXU=0 Radius=5 StartAngle=4.83268 EndAngle=7.85398
    g4: LineSegment [constr] StartX=37 StartY=6.5 StartZ=0 EndX=37 EndY=5 EndZ=0
    g5: LineSegment [constr] StartX=37.6 StartY=-6.47225 StartZ=0 EndX=37.6 EndY=-4.96387 EndZ=0
  constraints (16):
    c: PointOnObject(g0,g-6)
    c: PointOnObject(g0,g-6)
    c: Coincident(g1,g0)
    c: Coincident(g2,g0)
    c: Horizontal(g2)
    c: Coincident(g3,g2)
    c: Coincident(g3,g1)
    c: Coincident(g3,g-4)
    c: DistanceY(g0,g-6) = 1.5
    c: Coincident(g4,g-4)
    c: Coincident(g4,g2)
    c: Vertical(g4)
    c: DistanceY(g-6,g0) = 1.5
    c: Coincident(g5,g-5)
    c: Coincident(g5,g1)
    c: Vertical(g5)
FEATURE [PartDesign::Pocket] Pocket119
  BaseFeature = -> Pad173
  Direction = (0,0,1)
  Length = 0.5
  Length2 = 5
  Profile = -> Sketch265
  ReferenceAxis = -> Sketch265 [N_Axis]
  Refine = true
  Suppressed = false
  Type = 0
FEATURE [Sketcher::SketchObject] Sketch266
  ArcFitTolerance = 1e-06
  AttachmentSupport = -> [Pocket119]
  ExternalGeometry = -> [Pocket119]
  FullyConstrained = true
  MakeInternals = false
  MapMode = 5
  Placement = pos=(0,0,-6) rot=(1,0,0;3.14159rad)
  sketch-geometry (3):
    g0: ArcOfCircle CenterX=37 CenterY=0 CenterZ=0 NormalX=0 NormalY=0 NormalZ=1 AngleXU=0 Radius=4.34222 StartAngle=3.77496 EndAngle=8.5615
    g1: LineSegment StartX=33.5 StartY=3.3 StartZ=0 EndX=33.5 EndY=-2.57 EndZ=0
    g2: LineSegment StartX=34.1778 StartY=3.3 StartZ=0 EndX=33.5 EndY=3.3 EndZ=0
  constraints (9):
    c: DistanceY(g-4,g0) = 2.8
    c: DistanceY(g0,g-5) = 1.7
    c: PointOnObject(g0,g-6)
    c: Coincident(g1,g0)
    c: Coincident(g0,g-3)
    c: Coincident(g2,g0)
    c: Coincident(g2,g1)
    c: Horizontal(g2)
    c: PointOnObject(g1,g-6)
FEATURE [PartDesign::Pad] Pad174
  BaseFeature = -> Pocket119
  Direction = (0,0,-1)
  Length = 1.25
  Length2 = 10
  Profile = -> Sketch266
  ReferenceAxis = -> Sketch266 [N_Axis]
  Refine = true
  Suppressed = false
  Type = 0
FEATURE [Sketcher::SketchObject] Sketch267
  ArcFitTolerance = 1e-06
  AttachmentSupport = -> [Pad174]
  ExternalGeometry = -> [Pad174]
  FullyConstrained = true
  MakeInternals = false
  MapMode = 5
  Placement = pos=(0,0,-6.5) rot=(1,0,0;3.14159rad)
  sketch-geometry (17):
    g0: ArcOfCircle CenterX=36.7879 CenterY=6.49654 CenterZ=0 NormalX=0 NormalY=0 NormalZ=1 AngleXU=0 Radius=0.5 StartAngle=6.27735 EndAngle=9.41785
    g1: ArcOfCircle CenterX=36.7853 CenterY=-6.55898 CenterZ=0 NormalX=0 NormalY=0 NormalZ=1 AngleXU=0 Radius=0.5 StartAngle=3.24391 EndAngle=6.38834
    g2: ArcOfCircle CenterX=40.1188 CenterY=-5.70292 CenterZ=0 NormalX=0 NormalY=0 NormalZ=1 AngleXU=0 Radius=0.5 StartAngle=3.60356 EndAngle=6.82209
    g3: ArcOfCircle CenterX=40.1188 CenterY=5.70292 CenterZ=0 NormalX=0 NormalY=0 NormalZ=1 AngleXU=0 Radius=0.5 StartAngle=5.74428 EndAngle=8.96281
    g4: ArcOfCircle CenterX=42.5842 CenterY=3.32673 CenterZ=0 NormalX=0 NormalY=0 NormalZ=1 AngleXU=0 Radius=0.5 StartAngle=5.2112 EndAngle=8.42974
    g5: ArcOfCircle CenterX=42.5842 CenterY=-3.32673 CenterZ=0 NormalX=0 NormalY=0 NormalZ=1 AngleXU=0 Radius=0.5 StartAngle=4.13663 EndAngle=7.35517
    g6: ArcOfCircle CenterX=43.5 CenterY=0 CenterZ=0 NormalX=0 NormalY=0 NormalZ=1 AngleXU=0 Radius=0.5 StartAngle=4.67392 EndAngle=7.89245
    g7: LineSegment [constr] StartX=36.2879 StartY=6.5 StartZ=0 EndX=36.2879 EndY=-6.61005 EndZ=0
    g8: LineSegment [constr] StartX=39.6712 StartY=5.92578 StartZ=0 EndX=39.6712 EndY=-5.92578 EndZ=0
    g9: LineSegment [constr] StartX=42.3119 StartY=3.74612 StartZ=0 EndX=42.3119 EndY=-3.74612 EndZ=0
    g10: LineSegment StartX=36.2879 StartY=6.5 StartZ=0 EndX=37.2879 EndY=6.49362 EndZ=0
    g11: LineSegment StartX=39.6712 StartY=5.92578 StartZ=0 EndX=40.5479 EndY=5.44632 EndZ=0
    g12: LineSegment StartX=42.3119 StartY=3.74612 StartZ=0 EndX=42.8234 EndY=2.88765 EndZ=0
    g13: LineSegment StartX=43.4808 StartY=0.49963 StartZ=0 EndX=43.4808 EndY=-0.49963 EndZ=0
    g14: LineSegment StartX=42.8234 StartY=-2.88765 StartZ=0 EndX=42.3119 EndY=-3.74612 EndZ=0
    g15: LineSegment StartX=40.5479 StartY=-5.44632 StartZ=0 EndX=39.6712 EndY=-5.92578 EndZ=0
    g16: LineSegment StartX=37.2825 StartY=-6.5065 StartZ=0 EndX=36.2879 EndY=-6.61005 EndZ=0
  constraints (56):
    c: PointOnObject(g0,g-5)
    c: PointOnObject(g0,g-4)
    c: PointOnObject(g1,g-3)
    c: PointOnObject(g2,g-4)
    c: PointOnObject(g2,g-4)
    c: PointOnObject(g3,g-4)
    c: PointOnObject(g3,g-4)
    c: PointOnObject(g4,g-4)
    c: PointOnObject(g4,g-4)
    c: PointOnObject(g5,g-4)
    c: PointOnObject(g5,g-4)
    c: PointOnObject(g6,g-4)
    c: PointOnObject(g6,g-4)
    c: PointOnObject(g6,g-1)
    c: Diameter(g0) = 1
    c: Diameter(g3) = 1
    c: Diameter(g4) = 1
    c: Diameter(g6) = 1
    c: Diameter(g5) = 1
    c: Diameter(g2) = 1
    c: Diameter(g1) = 1
    c: PointOnObject(g6,g-4)
    c: PointOnObject(g4,g-4)
    c: PointOnObject(g3,g-4)
    c: PointOnObject(g0,g-4)
    c: PointOnObject(g5,g-4)
    c: PointOnObject(g2,g-4)
    c: PointOnObject(g1,g-3)
    c: Distance(g-3,g1) = 2.8
    c: PointOnObject(g1,g-3)
    c: Coincident(g7,g0)
    c: Coincident(g7,g1)
    c: Vertical(g7)
    c: Distance(g0,g3) = 2.45
    c: Distance(g3,g4) = 2.45
    c: Distance(g4,g6) = 2.47686
    c: Coincident(g8,g3)
    c: Coincident(g8,g2)
    c: Vertical(g8)
    c: Vertical(g4,g5)
    c: Coincident(g9,g4)
    c: Coincident(g9,g5)
    c: Coincident(g11,g3)
    c: Coincident(g11,g3)
    c: Coincident(g12,g4)
    c: Coincident(g12,g4)
    c: Coincident(g13,g6)
    c: Coincident(g13,g6)
    c: Coincident(g14,g5)
    c: Coincident(g14,g5)
    c: Coincident(g15,g2)
    c: Coincident(g15,g2)
    c: Coincident(g10,g0)
    c: Coincident(g10,g0)
    c: Coincident(g16,g1)
    c: Coincident(g16,g1)
FEATURE [PartDesign::Pad] Pad175
  BaseFeature = -> Pad174
  Direction = (0,0,-1)
  Length = 8
  Length2 = 10
  Profile = -> Sketch267
  ReferenceAxis = -> Sketch267 [N_Axis]
  Refine = true
  Reversed = true
  Suppressed = false
  Type = 0
FEATURE [Sketcher::SketchObject] Sketch268
  ArcFitTolerance = 1e-06
  AttachmentSupport = -> [Pad175]
  ExternalGeometry = -> [Pad175]
  FullyConstrained = true
  MakeInternals = false
  MapMode = 5
  Placement = pos=(0,0,-6.5) rot=(1,0,0;3.14159rad)
  sketch-geometry (4):
    g0: LineSegment StartX=43.4374 StartY=0.9 StartZ=0 EndX=43.4374 EndY=-0.9 EndZ=0
    g1: LineSegment StartX=43.4374 StartY=0.9 StartZ=0 EndX=45.5374 EndY=0.9 EndZ=0
    g2: LineSegment StartX=45.5374 StartY=0.9 StartZ=0 EndX=45.5374 EndY=-0.9 EndZ=0
    g3: LineSegment StartX=45.5374 StartY=-0.9 StartZ=0 EndX=43.4374 EndY=-0.9 EndZ=0
  constraints (12):
    c: PointOnObject(g0,g-3)
    c: PointOnObject(g0,g-4)
    c: Vertical(g0)
    c: DistanceY(g0,g0) = 1.8
    c: Coincident(g1,g0)
    c: Horizontal(g1)
    c: Coincident(g2,g1)
    c: Vertical(g2)
    c: Coincident(g3,g2)
    c: Coincident(g3,g0)
    c: Horizontal(g3)
    c: DistanceX(g1,g1) = 2.1
FEATURE [PartDesign::Pad] Pad176
  BaseFeature = -> Pad175
  Direction = (0,0,-1)
  Length = 4
  Length2 = 10
  Profile = -> Sketch268
  ReferenceAxis = -> Sketch268 [N_Axis]
  Refine = true
  Reversed = true
  Suppressed = false
  Type = 0
FEATURE [Sketcher::SketchObject] Sketch269
  ArcFitTolerance = 1e-06
  AttachmentSupport = -> [Pad176]
  ExternalGeometry = -> [Pad176]
  FullyConstrained = true
  MakeInternals = false
  MapMode = 5
  Placement = pos=(0,0,-6.5) rot=(1,0,0;3.14159rad)
  sketch-geometry (4):
    g0: LineSegment StartX=45.5374 StartY=0.9 StartZ=0 EndX=43.4374 EndY=0.9 EndZ=0
    g1: LineSegment StartX=43.4374 StartY=0.9 StartZ=0 EndX=43.4374 EndY=-0.9 EndZ=0
    g2: LineSegment StartX=43.4374 StartY=-0.9 StartZ=0 EndX=45.5374 EndY=-0.9 EndZ=0
    g3: LineSegment StartX=45.5374 StartY=-0.9 StartZ=0 EndX=45.5374 EndY=0.9 EndZ=0
  constraints (10):
    c: Coincident(g0,g1)
    c: Coincident(g1,g2)
    c: Coincident(g2,g3)
    c: Coincident(g3,g0)
    c: Horizontal(g0)
    c: Horizontal(g2)
    c: Vertical(g1)
    c: Vertical(g3)
    c: Coincident(g0,g-5)
    c: Coincident(g1,g-4)
FEATURE [PartDesign::Pad] Pad177
  BaseFeature = -> Pad176
  Direction = (0,0,-1)
  Length = 1.7
  Length2 = 10
  Profile = -> Sketch269
  ReferenceAxis = -> Sketch269 [N_Axis]
  Refine = true
  Suppressed = false
  Type = 0
FEATURE [Sketcher::SketchObject] Sketch270
  ArcFitTolerance = 1e-06
  AttachmentSupport = -> [Pad177]
  ExternalGeometry = -> [Pad177]
  FullyConstrained = true
  MakeInternals = false
  MapMode = 5
  Placement = pos=(0,0.9,0) rot=(0,0.707107,0.707107;3.14159rad)
  sketch-geometry (3):
    g0: LineSegment StartX=-43.4374 StartY=-8.2 StartZ=0 EndX=-44.0374 EndY=-8.2 EndZ=0
    g1: LineSegment StartX=-44.0374 StartY=-8.2 StartZ=0 EndX=-43.4374 EndY=-7.6 EndZ=0
    g2: LineSegment StartX=-43.4374 StartY=-7.6 StartZ=0 EndX=-43.4374 EndY=-8.2 EndZ=0
  constraints (8):
    c: Coincident(g0,g-4)
    c: PointOnObject(g0,g-4)
    c: Coincident(g1,g0)
    c: PointOnObject(g1,g-3)
    c: Coincident(g2,g1)
    c: Coincident(g2,g0)
    c: DistanceX(g-5,g0) = 1.5
    c: Angle(g0,g1) = 0.785398
FEATURE [PartDesign::Pocket] Pocket120
  BaseFeature = -> Pad177
  Direction = (0,-1,2e-16)
  Length = 5
  Length2 = 5
  Profile = -> Sketch270
  ReferenceAxis = -> Sketch270 [N_Axis]
  Refine = true
  Suppressed = false
  Type = 0
FEATURE [Sketcher::SketchObject] Sketch271
  ArcFitTolerance = 1e-06
  AttachmentSupport = -> [Pocket120]
  ExternalGeometry = -> [Pocket120]
  FullyConstrained = true
  MakeInternals = false
  MapMode = 5
  Placement = pos=(0,0.9,0) rot=(0,0.707107,0.707107;3.14159rad)
  sketch-geometry (3):
    g0: LineSegment StartX=-43.4374 StartY=-7.6 StartZ=0 EndX=-42.3374 EndY=-6.5 EndZ=0
    g1: LineSegment StartX=-42.3374 StartY=-6.5 StartZ=0 EndX=-43.4374 EndY=-6.5 EndZ=0
    g2: LineSegment StartX=-43.4374 StartY=-6.5 StartZ=0 EndX=-43.4374 EndY=-7.6 EndZ=0
  constraints (7):
    c: Coincident(g0,g-4)
    c: PointOnObject(g0,g-5)
    c: Coincident(g1,g0)
    c: Coincident(g1,g-7)
    c: Coincident(g2,g1)
    c: Coincident(g2,g0)
    c: Parallel(g0,g-4)
FEATURE [PartDesign::Pad] Pad178
  BaseFeature = -> Pocket120
  Direction = (0,1,-2e-16)
  Length = 1.8
  Length2 = 10
  Profile = -> Sketch271
  ReferenceAxis = -> Sketch271 [N_Axis]
  Refine = true
  Reversed = true
  Suppressed = false
  Type = 0
FEATURE [Sketcher::SketchObject] Sketch272
  ArcFitTolerance = 1e-06
  AttachmentSupport = -> [Pad178]
  ExternalGeometry = -> [Pad178]
  FullyConstrained = true
  MakeInternals = false
  MapMode = 5
  Placement = pos=(0,0,1.5) rot=(0,0,1;0rad)
  sketch-geometry (4):
    g0: ArcOfCircle CenterX=37 CenterY=0 CenterZ=0 NormalX=0 NormalY=0 NormalZ=1 AngleXU=0 Radius=4.25 StartAngle=4.14055 EndAngle=8.42582
    g1: LineSegment StartX=34.7 StartY=3.57386 StartZ=0 EndX=34.7 EndY=4.996 EndZ=0
    g2: LineSegment StartX=34.7 StartY=-3.57386 StartZ=0 EndX=34.7 EndY=-4.996 EndZ=0
    g3: ArcOfCircle CenterX=37 CenterY=0 CenterZ=0 NormalX=0 NormalY=0 NormalZ=1 AngleXU=0 Radius=5.5 StartAngle=4.28095 EndAngle=8.28542
  constraints (13):
    c: Coincident(g0,g-3)
    c: Diameter(g0) = 8.5
    c: Coincident(g1,g0)
    c: Coincident(g2,g0)
    c: Coincident(g3,g2)
    c: Coincident(g3,g1)
    c: Coincident(g0,g3)
    c: DistanceX(g-4,g2) = 1.2
    c: DistanceX(g-4,g1) = 1.2
    c: Vertical(g1)
    c: Vertical(g2)
    c: Radius(g-3) = 6.5
    c: Radius(g3) = 5.5
FEATURE [PartDesign::Pocket] Pocket121
  BaseFeature = -> Pad178
  Direction = (0,0,-1)
  Length = 6.5
  Length2 = 5
  Profile = -> Sketch272
  ReferenceAxis = -> Sketch272 [N_Axis]
  Refine = true
  Suppressed = false
  Type = 0
FEATURE [Sketcher::SketchObject] Sketch273
  ArcFitTolerance = 1e-06
  AttachmentSupport = -> [Pocket121]
  ExternalGeometry = -> [Pocket121]
  FullyConstrained = true
  MakeInternals = false
  MapMode = 5
  Placement = pos=(0,0,-7.25) rot=(1,0,0;3.14159rad)
  sketch-geometry (1):
    g0: Circle CenterX=37 CenterY=0 CenterZ=0 NormalX=0 NormalY=0 NormalZ=1 AngleXU=0 Radius=2.1
  constraints (2):
    c: Coincident(g0,g-3)
    c: Radius(g0) = 2.1
FEATURE [PartDesign::Pocket] Pocket122
  BaseFeature = -> Pocket121
  Direction = (0,0,1)
  Length = 4.7
  Length2 = 5
  Profile = -> Sketch273
  ReferenceAxis = -> Sketch273 [N_Axis]
  Refine = true
  Suppressed = false
  Type = 0
FEATURE [Sketcher::SketchObject] Sketch274
  ArcFitTolerance = 1e-06
  AttachmentSupport = -> [Pocket122]
  ExternalGeometry = -> [Pocket122]
  FullyConstrained = true
  MakeInternals = false
  MapMode = 5
  Placement = pos=(0,0,-2.55) rot=(1,0,0;3.14159rad)
  sketch-geometry (1):
    g0: Circle CenterX=37 CenterY=0 CenterZ=0 NormalX=0 NormalY=0 NormalZ=1 AngleXU=0 Radius=1.4
  constraints (2):
    c: Coincident(g0,g-3)
    c: Radius(g0) = 1.4
FEATURE [PartDesign::Pocket] Pocket123
  BaseFeature = -> Pocket122
  Direction = (0,0,1)
  Length = 5
  Length2 = 5
  Profile = -> Sketch274
  ReferenceAxis = -> Sketch274 [N_Axis]
  Refine = true
  Suppressed = false
  Type = 0
FEATURE [Sketcher::SketchObject] Sketch275
  ArcFitTolerance = 1e-06
  AttachmentSupport = -> [Pocket123]
  ExternalGeometry = -> [Pocket123]
  FullyConstrained = true
  MakeInternals = false
  MapMode = 5
  Placement = pos=(33.5,8e-15,0) rot=(0.57735,-0.57735,-0.57735;2.0944rad)
  sketch-geometry (1):
    g0: Circle CenterX=0 CenterY=-2.5 CenterZ=0 NormalX=0 NormalY=0 NormalZ=1 AngleXU=0 Radius=1.5
  constraints (5):
    c: DistanceX(g-4,g-4) = 13.37
    c: DistanceY(g-5,g-5) = 8
    c: PointOnObject(g0,g-2)
    c: Radius(g0) = 1.5
    c: DistanceY(g0,g-5) = 4
FEATURE [PartDesign::Pad] Pad179
  BaseFeature = -> Pocket123
  Direction = (-1,0,0)
  Length = 1.6
  Length2 = 10
  Profile = -> Sketch275
  ReferenceAxis = -> Sketch275 [N_Axis]
  Refine = true
  Suppressed = false
  Type = 0
FEATURE [Sketcher::SketchObject] Sketch276
  ArcFitTolerance = 1e-06
  AttachmentSupport = -> [Pad179]
  ExternalGeometry = -> [Pad179]
  FullyConstrained = true
  MakeInternals = false
  MapMode = 5
  Placement = pos=(31.9,0,0) rot=(0.57735,-0.57735,-0.57735;2.0944rad)
  sketch-geometry (1):
    g0: Circle CenterX=0 CenterY=-2.5 CenterZ=0 NormalX=0 NormalY=0 NormalZ=1 AngleXU=0 Radius=2.5
  constraints (2):
    c: Coincident(g0,g-3)
    c: Diameter(g0) = 5
FEATURE [PartDesign::Pad] Pad180
  BaseFeature = -> Pad179
  Direction = (-1,0,0)
  Length = 1.5
  Length2 = 10
  Profile = -> Sketch276
  ReferenceAxis = -> Sketch276 [N_Axis]
  Refine = true
  Suppressed = false
  Type = 0
FEATURE [PartDesign::Body] Body017  label="Left_Ankle"
  AllowCompound = false
  Group = -> [Binder009,Sketch264,Pad173,Sketch265,Pocket119,Sketch266,Pad174,Sketch267,Pad175,Sketch268,Pad176,Sketch269,Pad177,Sketch270,Pocket120,Sketch271,Pad178,Sketch272,Pocket121,Sketch273,Pocket122,Sketch274,Pocket123,Sketch275,Pad179,Sketch276,Pad180]
  Origin = -> Origin018
  Placement = pos=(53.7,-27.4,-19.5) rot=(0,-0.71,-0.71;3.14159rad)
  Tip = -> Pad180
COMPONENT P13 — recipe-attached ("Pre_Right_Foot", modeled in this document).
Construction recipe (the document's own serialized feature program — sketch geometry with constraints, then the solid features built on it; lengths are millimeters unless a unit is written):

FEATURE [PartDesign::SubShapeBinder] Binder010
  BindCopyOnChange = 0
  BindMode = 2
  ClaimChildren = false
  Context = -> Body018 [Binder010.]
  Fuse = false
  MakeFace = true
  OffsetFill = false
  OffsetIntersection = false
  OffsetJoinType = 0
  OffsetOpenResult = false
  PartialLoad = false
  Refine = true
  Relative = true
  _Version = 2
FEATURE [Sketcher::SketchObject] Sketch277
  ArcFitTolerance = 1e-06
  AttachmentSupport = -> [Binder010]
  ExternalGeometry = -> [Binder010]
  FullyConstrained = false
  MakeInternals = false
  MapMode = 5
  Placement = pos=(0,0,1.5) rot=(0,0,1;0rad)
  sketch-geometry (4):
    g0: LineSegment StartX=33.5 StartY=2.57971 StartZ=0 EndX=33.5 EndY=-2.42029 EndZ=0
    g1: LineSegment StartX=33.5 StartY=-2.42029 StartZ=0 EndX=40.5 EndY=-2.42029 EndZ=0
    g2: LineSegment StartX=40.5 StartY=-2.42029 StartZ=0 EndX=40.5 EndY=2.57971 EndZ=0
    g3: LineSegment StartX=40.5 StartY=2.57971 StartZ=0 EndX=33.5 EndY=2.57971 EndZ=0
  constraints (12):
    c: Coincident(g0,g1)
    c: Coincident(g1,g2)
    c: Coincident(g2,g3)
    c: Coincident(g3,g0)
    c: Vertical(g0)
    c: Vertical(g2)
    c: Horizontal(g1)
    c: Horizontal(g3)
    c: PointOnObject(g0,g-5)
    c: DistanceY(g2,g2) = 5
    c: DistanceX(g3,g3) = 7
    c: DistanceX(g0,g-4) = 3.5
FEATURE [PartDesign::Pad] Pad181
  Direction = (0,0,1)
  Length = 1
  Length2 = 10
  Profile = -> Sketch277
  ReferenceAxis = -> Sketch277 [N_Axis]
  Refine = true
  Suppressed = false
  Type = 0
FEATURE [Sketcher::SketchObject] Sketch278
  ArcFitTolerance = 1e-06
  AttachmentSupport = -> [Pad181]
  ExternalGeometry = -> [Pad181]
  FullyConstrained = true
  MakeInternals = false
  MapMode = 5
  Placement = pos=(0,0,2.5) rot=(0,0,1;0rad)
  sketch-geometry (4):
    g0: LineSegment StartX=33.5 StartY=4.07971 StartZ=0 EndX=33.5 EndY=-3.92029 EndZ=0
    g1: LineSegment StartX=33.5 StartY=-3.92029 StartZ=0 EndX=44.5 EndY=-3.92029 EndZ=0
    g2: LineSegment StartX=44.5 StartY=-3.92029 StartZ=0 EndX=44.5 EndY=4.07971 EndZ=0
    g3: LineSegment StartX=44.5 StartY=4.07971 StartZ=0 EndX=33.5 EndY=4.07971 EndZ=0
  constraints (13):
    c: Coincident(g0,g1)
    c: Coincident(g1,g2)
    c: Coincident(g2,g3)
    c: Coincident(g3,g0)
    c: Vertical(g0)
    c: Vertical(g2)
    c: Horizontal(g1)
    c: Horizontal(g3)
    c: PointOnObject(g-6,g0)
    c: DistanceY(g0,g0) = 8
    c: DistanceY(g-6,g-6) = 5
    c: DistanceY(g-6,g0) = 1.5
    c: DistanceX(g3,g3) = 11
FEATURE [PartDesign::Pad] Pad182
  BaseFeature = -> Pad181
  Direction = (0,0,1)
  Length = 7.8
  Length2 = 10
  Profile = -> Sketch278
  ReferenceAxis = -> Sketch278 [N_Axis]
  Refine = true
  Suppressed = false
  Type = 0
FEATURE [Sketcher::SketchObject] Sketch279
  ArcFitTolerance = 1e-06
  AttachmentSupport = -> [Pad182]
  ExternalGeometry = -> [Pad182]
  FullyConstrained = true
  MakeInternals = false
  MapMode = 5
  Placement = pos=(0,4.07971,0) rot=(0,0.707107,0.707107;3.14159rad)
  sketch-geometry (3):
    g0: LineSegment StartX=-33.5 StartY=2.5 StartZ=0 EndX=-33.5 EndY=10.3 EndZ=0
    g1: LineSegment StartX=-33.5 StartY=10.3 StartZ=0 EndX=-37.5 EndY=10.3 EndZ=0
    g2: LineSegment StartX=-37.5 StartY=10.3 StartZ=0 EndX=-33.5 EndY=2.5 EndZ=0
  constraints (7):
    c: Coincident(g0,g-3)
    c: Coincident(g0,g-4)
    c: Coincident(g1,g0)
    c: PointOnObject(g1,g-4)
    c: Coincident(g2,g1)
    c: Coincident(g2,g0)
    c: DistanceX(g-4,g1) = 7
FEATURE [PartDesign::Pocket] Pocket124
  BaseFeature = -> Pad182
  Direction = (0,-1,2e-16)
  Length = 8
  Length2 = 5
  Profile = -> Sketch279
  ReferenceAxis = -> Sketch279 [N_Axis]
  Refine = true
  Suppressed = false
  Type = 0
FEATURE [Sketcher::SketchObject] Sketch280
  ArcFitTolerance = 1e-06
  AttachmentSupport = -> [Pocket124]
  ExternalGeometry = -> [Pocket124]
  FullyConstrained = true
  MakeInternals = false
  MapMode = 5
  Placement = pos=(0,4.07971,0) rot=(0,0.707107,0.707107;3.14159rad)
  sketch-geometry (1):
    g0: Circle CenterX=-41 CenterY=6.4 CenterZ=0 NormalX=0 NormalY=0 NormalZ=1 AngleXU=0 Radius=2
  constraints (5):
    c: Diameter(g0) = 4
    c: DistanceY(g-3,g-3) = 7.8
    c: DistanceY(g0,g-3) = 3.9
    c: DistanceX(g-4,g-4) = 7
    c: DistanceX(g-4,g0) = 3.5
FEATURE [PartDesign::Pocket] Pocket125
  BaseFeature = -> Pocket124
  Direction = (0,-1,2e-16)
  Length = 3.3
  Length2 = 5
  Profile = -> Sketch280
  ReferenceAxis = -> Sketch280 [N_Axis]
  Refine = true
  Suppressed = false
  Type = 0
FEATURE [Sketcher::SketchObject] Sketch281
  ArcFitTolerance = 1e-06
  AttachmentSupport = -> [Pocket125]
  ExternalGeometry = -> [Pocket125]
  FullyConstrained = true
  MakeInternals = false
  MapMode = 5
  Placement = pos=(0,-3.92029,0) rot=(1,0,0;1.5708rad)
  sketch-geometry (1):
    g0: Circle CenterX=41 CenterY=6.4 CenterZ=0 NormalX=0 NormalY=0 NormalZ=1 AngleXU=0 Radius=2
  constraints (2):
    c: Coincident(g0,g-3)
    c: Equal(g0,g-3)
FEATURE [PartDesign::Pocket] Pocket126
  BaseFeature = -> Pocket125
  Direction = (0,1,-2e-16)
  Length = 3.3
  Length2 = 5
  Profile = -> Sketch281
  ReferenceAxis = -> Sketch281 [N_Axis]
  Refine = true
  Suppressed = false
  Type = 0
FEATURE [Sketcher::SketchObject] Sketch282
  ArcFitTolerance = 1e-06
  AttachmentSupport = -> [Pocket126]
  ExternalGeometry = -> [Pocket126]
  FullyConstrained = true
  MakeInternals = false
  MapMode = 5
  Placement = pos=(0,0,1.5) rot=(1,0,0;3.14159rad)
  sketch-geometry (1):
    g0: Circle CenterX=37 CenterY=0 CenterZ=0 NormalX=0 NormalY=0 NormalZ=1 AngleXU=0 Radius=0.9
  constraints (4):
    c: PointOnObject(g0,g-1)
    c: Radius(g0) = 0.9
    c: DistanceX(g-3,g-4) = 7
    c: DistanceX(g-3,g0) = 3.5
FEATURE [PartDesign::Pocket] Pocket127
  BaseFeature = -> Pocket126
  Direction = (0,0,1)
  Length = 5
  Length2 = 5
  Profile = -> Sketch282
  ReferenceAxis = -> Sketch282 [N_Axis]
  Refine = true
  Suppressed = false
  Type = 0
FEATURE [PartDesign::Pad] Pad183
  BaseFeature = -> Pocket127
  Direction = (1,0,0)
  Length = 0.5
  Length2 = 10
  Profile = -> Pocket127 [Face10]
  Refine = true
  Suppressed = false
  Type = 0
FEATURE [PartDesign::Fillet] Fillet013
  Base = -> Pad183 [Edge22,Edge4,Edge27,Edge23,Edge24,Edge5,Edge2,Edge3,Face1,Edge31,Edge6]
  BaseFeature = -> Pad183
  Radius = 0.5
  Refine = true
  SupportTransform = false
  Suppressed = false
  UseAllEdges = false
FEATURE [PartDesign::Body] Body018  label="Left_Foot"
  AllowCompound = false
  Group = -> [Binder010,Sketch277,Pad181,Sketch278,Pad182,Sketch279,Pocket124,Sketch280,Pocket125,Sketch281,Pocket126,Sketch282,Pocket127,Pad183,Fillet013]
  Origin = -> Origin019
  Placement = pos=(53.7,-27.4,-19.5) rot=(0,-0.71,-0.71;3.14159rad)
  Tip = -> Fillet013
